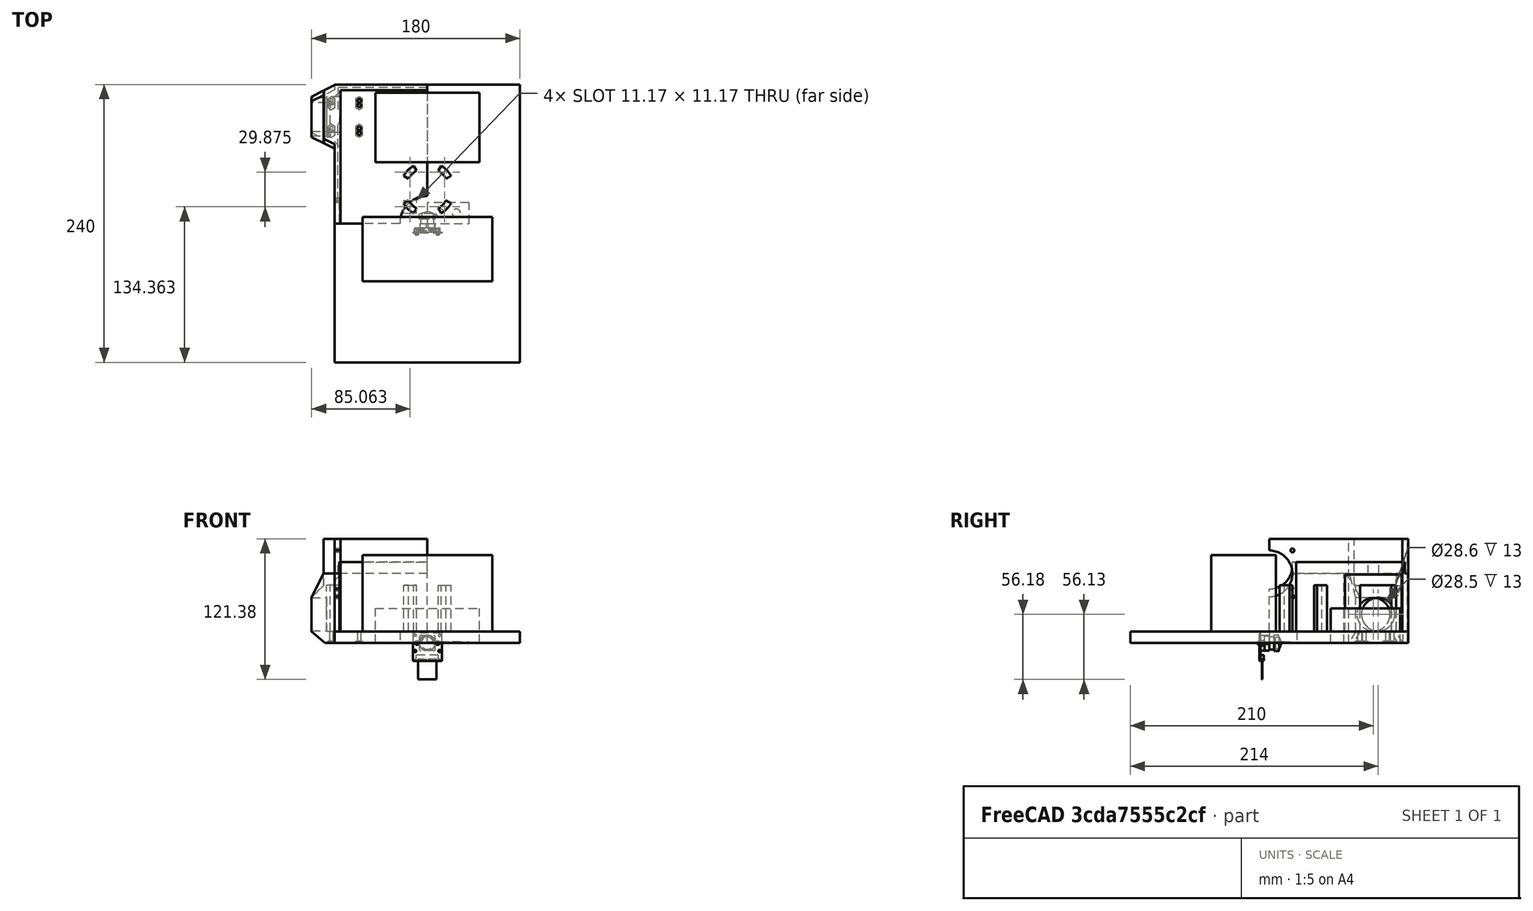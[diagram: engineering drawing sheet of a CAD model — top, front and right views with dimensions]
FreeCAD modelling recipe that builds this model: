
FCSTD DOCUMENT  (FreeCAD 0.18R16146 (Git))
Label: goat-ver3
License: All rights reserved
LicenseURL: http://en.wikipedia.org/wiki/All_rights_reserved
objects: Sketcher::SketchObject×31, PartDesign::Pocket×19, PartDesign::Pad×11, PartDesign::Body×8, Part::Feature×8, Spreadsheet::Sheet×3, PartDesign::Mirrored×3, Mesh::Feature×2, PartDesign::Chamfer×1, PartDesign::PolarPattern×1, App::Part×1, PartDesign::Plane×1, PartDesign::MultiTransform×1
note: 114 computed .brp shape members not serialized (recipe doc carries the construction recipe); baked Part::Feature solids carry a one-line shape summary decoded from their .brp

FEATURE [Spreadsheet::Sheet] Spreadsheet  label="config"
  cells = A1=NAME; B1=VALUE; A2=car_length; B2(car_length)==240mm; A3=car_width; B3==160mm; A4=lower_car_height; B4(lower_car_height)==90mm; A5=upper_car_height; B5(upper_car_height)==50mm; A6=car_floor_thickness; B6(car_floor_thickness)==10mm; A7=car_wall_thickness; B7(car_wall_thickness)==5mm; A8=car_connect_space; B8(car_connect_space)==0.5mm; A9=car_connect_magnet_radius; B9(car_connect_magnet_radius)==7.05mm; A10=car_connect_height; B10==10mm; A11=ENGINES; B11(ENGINES)=; A12=engine_radius; B12(engine_radius)==14.3mm; A13=engine_placement_from_base; B13(engine_placement_from_base)==config.car_length / 2 - 26mm; A14=engine_lift_from_base; B14(engine_lift_from_base)==0.5mm; A15=engine_house_height; B15(engine_house_height)==40mm; A16=engine_house_width; B16(engine_house_width)==30.9mm; A17=engine_house_length; B17(engine_house_length)==35mm; A18=engine_front_length; B18(engine_front_length)==20mm; A19=engine_screw_sepdist; B19(engine_screw_sepdist)==24mm; A20=engine_screw_hole_radius; B20(engine_screw_hole_radius)==1.65mm; A21=engine_screw_nut_radius; B21(engine_screw_nut_radius)==3.55mm; A22=engine_screw_nut_depth; B22(engine_screw_nut_depth)==1.8mm; A23=engine_pocket_house; B23(engine_pocket_house)==12mm; A24=FAN; A25=fan_length; B25(fan_length)==50mm; A26=fan_insert_slit_length; B26(fan_insert_slit_length)==46mm; A27=fan_screw_sepdist; B27(fan_screw_sepdist)==40mm; A28=fan_insert_depth; B28(fan_insert_depth)==1mm; A29=fan_screw_hole_radius; B29(fan_screw_hole_radius)==1.65mm; A30=fan_screw_nut_radius; B30(fan_screw_nut_radius)==3.55mm; A31=GRASSCUTTER; A32=grasscutter_motor_radius; B32(grasscutter_motor_radius)==18.7mm; A33=grasscutter_inner_radius; B33(grasscutter_inner_radius)==7.5mm; A34=grasscutter_inner_depth; B34(grasscutter_inner_depth)==4.55mm; A35=grasscutter_wall_height; B35(grasscutter_wall_height)==50mm; A36=grasscutter_screw_radius; B36(grasscutter_screw_radius)==13.5mm; A37=grasscutter_screw_circledist; B37(grasscutter_screw_circledist)==2 * 3.14 * B36 / 6; A38=grasscutter_screw_hole_radius; B38(grasscutter_screw_hole_radius)==1.52mm; A39=grasscutter_screw_nut_radius; B39(grasscutter_screw_nut_radius)==2.5mm; A40=grasscutter_screw_nut_depth; B40(grasscutter_screw_nut_depth)==1mm; A41=grasscutter_placement_yaxis; B41(grasscutter_placement_yaxis)==config.rpi_placement_yaxis - config.grasscutter_motor_radius - 5mm; A44=BATTERY; A45=battery_length; B45(battery_length)==112mm; A46=battery_width; B46(battery_width)==55.7mm; A47=battery_height; B47(battery_height)==66mm; A48=battery_placement_yaxis; B48(battery_placement_yaxis)==-config.battery_width + config.grasscutter_placement_yaxis - config.grasscutter_motor_radius - 5mm; A50=RASPBERRY; A51=rpi_height; B51(rpi_height)==30mm; A52=rpi_width; B52(rpi_width)==60mm; A53=rpi_length; B53(rpi_length)==90mm; A54=rpi_placement_yaxis; B54(rpi_placement_yaxis)==config.car_length / 2 - config.rpi_width - config.car_wall_thickness - 2mm; A57=CAMERA; B57(CAMERA)=; C57=https://www.raspberrypi-spy.co.uk/2013/05/pi-camera-module-mechanical-dimensions/; A59=camera_placement_yaxis; B59(camera_placement_yaxis)==120mm; A60=camera_placement_zaxis; B60==60mm; A61=camera_support_start_zaxis; B61(camera_support_start_zaxis)==50mm; A62=camera_tilt_angle; B62(camera_tilt_angle)=15; A63=camera_width; B63(camera_width)==24mm; A64=camera_height; B64(camera_height)==25mm; A65=camera_lens_length; B65(camera_lens_length)==13mm; A66=camera_lens_radius; B66(camera_lens_radius)==7.5mm; A67=camera_screw1_height; B67(camera_screw1_height)==9.5mm; A68=camera_screw2_height; B68(camera_screw2_height)==9.5mm + 12.5mm; A69=camera_screw_dist_apart; B69(camera_screw_dist_apart)==21mm; A70=camera_screw_radius; B70(camera_screw_radius)==1.1mm; A71=camera_screw_depth; B71==3mm; C71=length of taps to hold the camera; A72=camera_lens_placement_height; B72==24mm - 9.5mm
FEATURE [Sketcher::SketchObject] Sketch
  MapMode = 5
  Support = -> [XY_Plane]
  expr: Constraints[10] = config.car_width / 2
  expr: Constraints[9] = config.car_length / 2
  sketch-geometry (4):
    g0: LineSegment StartX=0 StartY=0 StartZ=0 EndX=-80 EndY=0 EndZ=0
    g1: LineSegment StartX=-80 StartY=0 StartZ=0 EndX=-80 EndY=120 EndZ=0
    g2: LineSegment StartX=-80 StartY=120 StartZ=0 EndX=0 EndY=120 EndZ=0
    g3: LineSegment StartX=0 StartY=120 StartZ=0 EndX=0 EndY=0 EndZ=0
  constraints (11):
    c: Coincident(g0,g1)
    c: Coincident(g1,g2)
    c: Coincident(g2,g3)
    c: Coincident(g3,g0)
    c: Horizontal(g0)
    c: Horizontal(g2)
    c: Vertical(g1)
    c: Vertical(g3)
    c: Coincident(g0,g-1)
    c: Distance(g3) = 120
    c: Distance(g2) = 80
FEATURE [PartDesign::Pad] Pad  label="pad-floor"
  Length = 10
  Length2 = 100
  Profile = -> Sketch
  Type = 0
  expr: Length = config.car_floor_thickness
FEATURE [Sketcher::SketchObject] Sketch002
  MapMode = 5
  Support = -> [XY_Plane]
  expr: Constraints[34] = config.engine_placement_from_base
  expr: Constraints[28] = config.car_width / 2
  expr: Constraints[26] = config.car_wall_thickness
  expr: Constraints[27] = config.car_wall_thickness
  expr: Constraints[25] = config.engine_front_length
  expr: Constraints[24] = config.engine_front_length / 2
  expr: Constraints[23] = config.engine_house_width
  expr: Constraints[21] = config.car_length / 2
  expr: Constraints[20] = config.car_width / 2
  sketch-geometry (12):
    g0: LineSegment StartX=0 StartY=115 StartZ=0 EndX=0 EndY=120 EndZ=0
    g1: LineSegment StartX=0 StartY=120 StartZ=0 EndX=-80 EndY=120 EndZ=0
    g2: LineSegment StartX=-80 StartY=120 StartZ=0 EndX=-80 EndY=119.45 EndZ=0
    g3: LineSegment StartX=-80 StartY=119.45 StartZ=0 EndX=-100 EndY=109.45 EndZ=0
    g4: LineSegment StartX=-100 StartY=109.45 StartZ=0 EndX=-100 EndY=78.55 EndZ=0
    g5: LineSegment StartX=-100 StartY=78.55 StartZ=0 EndX=-80 EndY=68.55 EndZ=0
    g6: LineSegment StartX=-80 StartY=68.55 StartZ=0 EndX=-80 EndY=0 EndZ=0
    g7: LineSegment StartX=-80 StartY=0 StartZ=0 EndX=-75 EndY=0 EndZ=0
    g8: LineSegment StartX=-75 StartY=0 StartZ=0 EndX=-75 EndY=115 EndZ=0
    g9: LineSegment StartX=-75 StartY=115 StartZ=0 EndX=0 EndY=115 EndZ=0
    g10: LineSegment [constr] StartX=-100 StartY=78.55 StartZ=0 EndX=-100 EndY=94 EndZ=0
    g11: LineSegment [constr] StartX=-100 StartY=94 StartZ=0 EndX=-100 EndY=109.45 EndZ=0
  constraints (35):
    c: PointOnObject(g0,g-2)
    c: Vertical(g0)
    c: Coincident(g0,g1)
    c: Horizontal(g1)
    c: Coincident(g1,g2)
    c: Vertical(g2)
    c: Coincident(g2,g3)
    c: Coincident(g3,g4)
    c: Vertical(g4)
    c: Coincident(g4,g5)
    c: Coincident(g5,g6)
    c: PointOnObject(g6,g-1)
    c: Vertical(g6)
    c: Coincident(g6,g7)
    c: PointOnObject(g7,g-1)
    c: Coincident(g7,g8)
    c: Vertical(g8)
    c: Coincident(g8,g9)
    c: Coincident(g9,g0)
    c: Horizontal(g9)
    c: Distance(g1) = 80
    c: Distance(g-1,g0) = 120
    c: Equal(g3,g5)
    c: Distance(g4) = 30.9
    c: DistanceY(g3,g2) = 10
    c: DistanceX(g3,g2) = 20
    c: Distance(g0,g0) = 5
    c: Distance(g6,g7) = 5
    c: Distance(g-1,g6) = 80
    c: Coincident(g4,g10)
    c: PointOnObject(g10,g4)
    c: Coincident(g10,g11)
    c: Coincident(g11,g3)
    c: Equal(g10,g11)
    c: DistanceY(g-1,g10) = 94
FEATURE [PartDesign::Pad] Pad001  label="pad-walls"
  BaseFeature = -> Pad
  Length = 90
  Length2 = 100
  Profile = -> Sketch002
  Type = 0
  expr: Length = config.lower_car_height
FEATURE [Sketcher::SketchObject] Sketch003
  AttachmentOffset = pos=(0,0,-75) rot=(0,0,1;0rad)
  MapMode = 5
  Placement = pos=(-75,1.67e-14,-1.67e-14) rot=(0.57735,0.57735,0.57735;2.0944rad)
  Support = -> [YZ_Plane]
  expr: AttachmentOffset.Base.y = 0
  expr: Constraints[16] = config.engine_placement_from_base
  expr: Constraints[10] = config.car_floor_thickness
  expr: Constraints[9] = config.engine_house_height
  expr: Constraints[8] = config.engine_house_width
  sketch-geometry (6):
    g0: LineSegment StartX=78.55 StartY=50 StartZ=0 EndX=109.45 EndY=50 EndZ=0
    g1: LineSegment StartX=109.45 StartY=50 StartZ=0 EndX=109.45 EndY=10 EndZ=0
    g2: LineSegment StartX=109.45 StartY=10 StartZ=0 EndX=78.55 EndY=10 EndZ=0
    g3: LineSegment StartX=78.55 StartY=10 StartZ=0 EndX=78.55 EndY=50 EndZ=0
    g4: LineSegment [constr] StartX=78.55 StartY=10 StartZ=0 EndX=94 EndY=10 EndZ=0
    g5: LineSegment [constr] StartX=94 StartY=10 StartZ=0 EndX=109.45 EndY=10 EndZ=0
  constraints (17):
    c: Coincident(g0,g1)
    c: Coincident(g1,g2)
    c: Coincident(g2,g3)
    c: Coincident(g3,g0)
    c: Horizontal(g0)
    c: Horizontal(g2)
    c: Vertical(g1)
    c: Vertical(g3)
    c: Distance(g0) = 30.9
    c: Distance(g3) = 40
    c: DistanceY(g-1,g2) = 10
    c: Coincident(g2,g4)
    c: Horizontal(g4)
    c: Coincident(g4,g5)
    c: Coincident(g5,g1)
    c: Equal(g4,g5)
    c: DistanceX(g-1,g4) = 94
FEATURE [PartDesign::Pocket] Pocket  label="pocket-engine-house"
  BaseFeature = -> Pad001
  Length = 12
  Length2 = 100
  Profile = -> Sketch003
  Type = 0
  expr: Length = config.engine_pocket_house
FEATURE [PartDesign::Pocket] Pocket001  label="pocket-engine-radius"
  BaseFeature = -> Pocket
  Length = 5
  Length2 = 100
  Type = 1
FEATURE [Sketcher::SketchObject] Sketch005
  MapMode = 5
  Support = -> [XY_Plane]
  expr: Constraints[24] = config.car_width / 2 - config.car_wall_thickness + config.engine_pocket_house
  expr: Constraints[20] = config.engine_screw_hole_radius
  expr: Constraints[15] = config.engine_placement_from_base
  expr: Constraints[14] = config.engine_screw_sepdist
  expr: Constraints[10] = config.engine_screw_hole_radius * 2.5
  sketch-geometry (10):
    g0: LineSegment [constr] StartX=-82.875 StartY=106 StartZ=0 EndX=-58.875 EndY=106 EndZ=0
    g1: LineSegment [constr] StartX=-58.875 StartY=106 StartZ=0 EndX=-58.875 EndY=82 EndZ=0
    g2: LineSegment [constr] StartX=-58.875 StartY=82 StartZ=0 EndX=-82.875 EndY=82 EndZ=0
    g3: LineSegment [constr] StartX=-82.875 StartY=82 StartZ=0 EndX=-82.875 EndY=106 EndZ=0
    g4: LineSegment [constr] StartX=-82.875 StartY=106 StartZ=0 EndX=-87 EndY=94 EndZ=0
    g5: LineSegment [constr] StartX=-87 StartY=94 StartZ=0 EndX=-82.875 EndY=82 EndZ=0
    g6: Circle CenterX=-82.875 CenterY=106 CenterZ=0 NormalX=0 NormalY=0 NormalZ=1 AngleXU=0 Radius=1.65
    g7: Circle CenterX=-58.875 CenterY=106 CenterZ=0 NormalX=0 NormalY=0 NormalZ=1 AngleXU=0 Radius=1.65
    g8: Circle CenterX=-58.875 CenterY=82 CenterZ=0 NormalX=0 NormalY=0 NormalZ=1 AngleXU=0 Radius=1.65
    g9: Circle CenterX=-82.875 CenterY=82 CenterZ=0 NormalX=0 NormalY=0 NormalZ=1 AngleXU=0 Radius=1.65
  constraints (25):
    c: Coincident(g0,g1)
    c: Coincident(g1,g2)
    c: Coincident(g2,g3)
    c: Coincident(g3,g0)
    c: Horizontal(g0)
    c: Vertical(g1)
    c: Coincident(g0,g4)
    c: Coincident(g4,g5)
    c: Coincident(g5,g2)
    c: Equal(g5,g4)
    c: DistanceX(g4,g0) = 4.125
    c: Equal(g0,g3)
    c: Equal(g3,g2)
    c: Equal(g2,g1)
    c: Distance(g1) = 24
    c: DistanceY(g-1,g4) = 94
    c: Coincident(g6,g0)
    c: Coincident(g7,g0)
    c: Coincident(g8,g1)
    c: Coincident(g9,g2)
    c: Radius(g6) = 1.65
    c: Equal(g6,g7)
    c: Equal(g6,g8)
    c: Equal(g6,g9)
    c: DistanceX(g4,g-1) = 87
FEATURE [PartDesign::Pocket] Pocket002  label="pocket-engine-screw"
  BaseFeature = -> Pocket001
  Length = 10
  Length2 = 100
  Profile = -> Sketch005
  Reversed = true
  Type = 0
  expr: Length = config.car_floor_thickness
FEATURE [Sketcher::SketchObject] Sketch006
  MapMode = 5
  Support = -> [XY_Plane]
  expr: Constraints[74] = config.engine_screw_nut_radius
  expr: Constraints[14] = config.engine_screw_sepdist
  expr: Constraints[16] = config.car_width / 2 - config.car_wall_thickness + config.engine_pocket_house
  expr: Constraints[10] = config.engine_screw_hole_radius * 2.5
  expr: Constraints[15] = config.engine_placement_from_base
  sketch-geometry (34):
    g0: LineSegment [constr] StartX=-82.875 StartY=106 StartZ=0 EndX=-58.875 EndY=106 EndZ=0
    g1: LineSegment [constr] StartX=-58.875 StartY=106 StartZ=0 EndX=-58.875 EndY=82 EndZ=0
    g2: LineSegment [constr] StartX=-58.875 StartY=82 StartZ=0 EndX=-82.875 EndY=82 EndZ=0
    g3: LineSegment [constr] StartX=-82.875 StartY=82 StartZ=0 EndX=-82.875 EndY=106 EndZ=0
    g4: LineSegment [constr] StartX=-82.875 StartY=106 StartZ=0 EndX=-87 EndY=94 EndZ=0
    g5: LineSegment [constr] StartX=-87 StartY=94 StartZ=0 EndX=-82.875 EndY=82 EndZ=0
    g6: LineSegment StartX=-79.8006 StartY=107.775 StartZ=0 EndX=-82.875 EndY=109.55 EndZ=0
    g7: LineSegment StartX=-82.875 StartY=109.55 StartZ=0 EndX=-85.9494 EndY=107.775 EndZ=0
    g8: LineSegment StartX=-85.9494 StartY=107.775 StartZ=0 EndX=-85.9494 EndY=104.225 EndZ=0
    g9: LineSegment StartX=-85.9494 StartY=104.225 StartZ=0 EndX=-82.875 EndY=102.45 EndZ=0
    g10: LineSegment StartX=-82.875 StartY=102.45 StartZ=0 EndX=-79.8006 EndY=104.225 EndZ=0
    g11: LineSegment StartX=-79.8006 StartY=104.225 StartZ=0 EndX=-79.8006 EndY=107.775 EndZ=0
    g12: Circle [constr] CenterX=-82.875 CenterY=106 CenterZ=0 NormalX=0 NormalY=0 NormalZ=1 AngleXU=0 Radius=3.55
    g13: LineSegment StartX=-55.8006 StartY=107.775 StartZ=0 EndX=-58.875 EndY=109.55 EndZ=0
    g14: LineSegment StartX=-58.875 StartY=109.55 StartZ=0 EndX=-61.9494 EndY=107.775 EndZ=0
    g15: LineSegment StartX=-61.9494 StartY=107.775 StartZ=0 EndX=-61.9494 EndY=104.225 EndZ=0
    g16: LineSegment StartX=-61.9494 StartY=104.225 StartZ=0 EndX=-58.875 EndY=102.45 EndZ=0
    g17: LineSegment StartX=-58.875 StartY=102.45 StartZ=0 EndX=-55.8006 EndY=104.225 EndZ=0
    g18: LineSegment StartX=-55.8006 StartY=104.225 StartZ=0 EndX=-55.8006 EndY=107.775 EndZ=0
    g19: Circle [constr] CenterX=-58.875 CenterY=106 CenterZ=0 NormalX=0 NormalY=0 NormalZ=1 AngleXU=0 Radius=3.55
    g20: LineSegment StartX=-58.875 StartY=85.55 StartZ=0 EndX=-61.9494 EndY=83.775 EndZ=0
    g21: LineSegment StartX=-61.9494 StartY=83.775 StartZ=0 EndX=-61.9494 EndY=80.225 EndZ=0
    g22: LineSegment StartX=-61.9494 StartY=80.225 StartZ=0 EndX=-58.875 EndY=78.45 EndZ=0
    g23: LineSegment StartX=-58.875 StartY=78.45 StartZ=0 EndX=-55.8006 EndY=80.225 EndZ=0
    g24: LineSegment StartX=-55.8006 StartY=80.225 StartZ=0 EndX=-55.8006 EndY=83.775 EndZ=0
    g25: LineSegment StartX=-55.8006 StartY=83.775 StartZ=0 EndX=-58.875 EndY=85.55 EndZ=0
    g26: Circle [constr] CenterX=-58.875 CenterY=82 CenterZ=0 NormalX=0 NormalY=0 NormalZ=1 AngleXU=0 Radius=3.55
    g27: LineSegment StartX=-79.8006 StartY=83.775 StartZ=0 EndX=-82.875 EndY=85.55 EndZ=0
    g28: LineSegment StartX=-82.875 StartY=85.55 StartZ=0 EndX=-85.9494 EndY=83.775 EndZ=0
    g29: LineSegment StartX=-85.9494 StartY=83.775 StartZ=0 EndX=-85.9494 EndY=80.225 EndZ=0
    g30: LineSegment StartX=-85.9494 StartY=80.225 StartZ=0 EndX=-82.875 EndY=78.45 EndZ=0
    g31: LineSegment StartX=-82.875 StartY=78.45 StartZ=0 EndX=-79.8006 EndY=80.225 EndZ=0
    g32: LineSegment StartX=-79.8006 StartY=80.225 StartZ=0 EndX=-79.8006 EndY=83.775 EndZ=0
    g33: Circle [constr] CenterX=-82.875 CenterY=82 CenterZ=0 NormalX=0 NormalY=0 NormalZ=1 AngleXU=0 Radius=3.55
  constraints (81):
    c: Coincident(g0,g1)
    c: Coincident(g1,g2)
    c: Coincident(g2,g3)
    c: Coincident(g3,g0)
    c: Horizontal(g0)
    c: Vertical(g1)
    c: Coincident(g0,g4)
    c: Coincident(g4,g5)
    c: Coincident(g5,g2)
    c: Equal(g5,g4)
    c: DistanceX(g4,g0) = 4.125
    c: Equal(g0,g3)
    c: Equal(g3,g2)
    c: Equal(g2,g1)
    c: Distance(g1) = 24
    c: DistanceY(g-1,g4) = 94
    c: DistanceX(g4,g-1) = 87
    c: Coincident(g6,g7)
    c: Coincident(g7,g8)
    c: Coincident(g8,g9)
    c: Coincident(g9,g10)
    c: Coincident(g10,g11)
    c: Coincident(g11,g6)
    c: Equal(g6, g7-g11) x5
    c: PointOnObject(g6,g12)
    c: PointOnObject(g7,g12)
    c: PointOnObject(g8,g12)
    c: PointOnObject(g9,g12)
    c: PointOnObject(g10,g12)
    c: PointOnObject(g11,g12)
    c: Coincident(g12,g0)
    c: Coincident(g13,g14)
    c: Coincident(g14,g15)
    c: Coincident(g15,g16)
    c: Coincident(g16,g17)
    c: Coincident(g17,g18)
    c: Coincident(g18,g13)
    c: Equal(g13, g14-g18) x5
    c: PointOnObject(g13,g19)
    c: PointOnObject(g14,g19)
    c: PointOnObject(g15,g19)
    c: PointOnObject(g16,g19)
    c: PointOnObject(g17,g19)
    c: PointOnObject(g18,g19)
    c: Coincident(g19,g0)
    c: Coincident(g20,g21)
    c: Coincident(g21,g22)
    c: Coincident(g22,g23)
    c: Coincident(g23,g24)
    c: Coincident(g24,g25)
    c: Coincident(g25,g20)
    c: Equal(g20, g21-g25) x5
    c: PointOnObject(g20,g26)
    c: PointOnObject(g21,g26)
    c: PointOnObject(g22,g26)
    c: PointOnObject(g23,g26)
    c: PointOnObject(g24,g26)
    c: PointOnObject(g25,g26)
    c: Coincident(g26,g1)
    c: Vertical(g8)
    c: Vertical(g21)
    c: Vertical(g15)
    c: Radius(g26) = 3.55
    c: Equal(g26,g19)
    c: Equal(g26,g12)
    c: Coincident(g27,g28)
    c: Coincident(g28,g29)
    c: Coincident(g29,g30)
    c: Coincident(g30,g31)
    c: Coincident(g31,g32)
    c: Coincident(g32,g27)
    c: Equal(g27, g28-g32) x5
    c: PointOnObject(g27,g33)
    c: PointOnObject(g28,g33)
    c: PointOnObject(g29,g33)
    c: PointOnObject(g30,g33)
    c: PointOnObject(g31,g33)
    c: PointOnObject(g32,g33)
    c: Coincident(g33,g2)
    c: Vertical(g29)
    c: Equal(g33,g12)
FEATURE [PartDesign::Pocket] Pocket003  label="pocket-engine-nut"
  BaseFeature = -> Pocket002
  Length = 1.8
  Length2 = 100
  Profile = -> Sketch006
  Reversed = true
  Type = 0
FEATURE [Sketcher::SketchObject] Sketch007
  MapMode = 5
  Placement = pos=(0,0,0) rot=(1,0,0;1.5708rad)
  Support = -> [XZ_Plane]
  expr: Constraints[17] = config.car_floor_thickness + 2 * config.engine_radius + config.engine_lift_from_base * 2
  expr: Constraints[16] = config.car_width / 2 + config.engine_pocket_house * 0.8
  expr: Constraints[10] = config.car_floor_thickness
  expr: Constraints[13] = config.lower_car_height
  expr: Constraints[12] = config.car_width / 2 + config.engine_front_length
  sketch-geometry (6):
    g0: LineSegment StartX=-89.6 StartY=90 StartZ=0 EndX=-100 EndY=39.6 EndZ=0
    g1: LineSegment StartX=-100 StartY=39.6 StartZ=0 EndX=-100 EndY=90 EndZ=0
    g2: LineSegment StartX=-100 StartY=90 StartZ=0 EndX=-89.6 EndY=90 EndZ=0
    g3: LineSegment StartX=-88.4 StartY=0 StartZ=0 EndX=-100 EndY=10 EndZ=0
    g4: LineSegment StartX=-100 StartY=10 StartZ=0 EndX=-100 EndY=0 EndZ=0
    g5: LineSegment StartX=-100 StartY=0 StartZ=0 EndX=-88.4 EndY=0 EndZ=0
  constraints (18):
    c: Coincident(g0,g1)
    c: Vertical(g1)
    c: Coincident(g1,g2)
    c: Coincident(g2,g0)
    c: Horizontal(g2)
    c: PointOnObject(g3,g-1)
    c: Coincident(g3,g4)
    c: PointOnObject(g4,g-1)
    c: Coincident(g4,g5)
    c: Coincident(g5,g3)
    c: Distance(g4) = 10
    c: DistanceX(g4,g-1) = 100
    c: DistanceX(g1,g-1) = 100
    c: DistanceY(g-1,g1) = 90
    c: DistanceX(g3,g-1) = 88.4
    c: Vertical(g4)
    c: DistanceX(g0,g-1) = 89.6
    c: DistanceY(g4,g0) = 39.6
FEATURE [PartDesign::Pocket] Pocket004  label="pocket-trim-engine-house"
  BaseFeature = -> Pocket003
  Length = 5
  Length2 = 100
  Profile = -> Sketch007
  Type = 1
FEATURE [Sketcher::SketchObject] Sketch009
  MapMode = 5
  Support = -> [XY_Plane]
  expr: Constraints[0] = config.grasscutter_motor_radius + config.car_wall_thickness
  sketch-geometry (1):
    g0: Circle CenterX=0 CenterY=0 CenterZ=0 NormalX=0 NormalY=0 NormalZ=1 AngleXU=0 Radius=23.7
  constraints (1):
    c: Radius(g0) = 23.7
FEATURE [PartDesign::Pocket] Pocket005  label="pocket-for-grasscutter"
  BaseFeature = -> Pocket004
  Length = 5
  Length2 = 100
  Profile = -> Sketch009
  Reversed = true
  Type = 1
FEATURE [Sketcher::SketchObject] Sketch014
  AttachmentOffset = pos=(0,0,90) rot=(0,0,1;0rad)
  MapMode = 5
  Placement = pos=(0,0,90) rot=(0,0,1;0rad)
  Support = -> [XY_Plane]
  expr: Constraints[26] = config.car_connect_magnet_radius + 0.5mm
  expr: Constraints[25] = config.engine_placement_from_base
  expr: Constraints[23] = config.car_connect_magnet_radius
  expr: Constraints[17] = (config.car_wall_thickness - config.car_connect_space) / 2
  expr: AttachmentOffset.Base.z = config.lower_car_height
  expr: Constraints[16] = config.car_length / 2 - config.car_wall_thickness
  expr: Constraints[15] = config.car_width / 2 - config.car_wall_thickness
  expr: Constraints[13] = (config.car_wall_thickness - config.car_connect_space) / 2
  sketch-geometry (9):
    g0: LineSegment StartX=0 StartY=115 StartZ=0 EndX=0 EndY=117.25 EndZ=0
    g1: LineSegment StartX=0 StartY=117.25 StartZ=0 EndX=-77.25 EndY=117.25 EndZ=0
    g2: LineSegment StartX=-77.25 StartY=117.25 StartZ=0 EndX=-77.25 EndY=98.6489 EndZ=0
    g3: LineSegment StartX=-77.25 StartY=0 StartZ=0 EndX=-75 EndY=0 EndZ=0
    g4: LineSegment StartX=-75 StartY=0 StartZ=0 EndX=-75 EndY=115 EndZ=0
    g5: LineSegment StartX=-75 StartY=115 StartZ=0 EndX=0 EndY=115 EndZ=0
    g6: LineSegment StartX=-77.25 StartY=0 StartZ=0 EndX=-77.25 EndY=89.3511 EndZ=0
    g7: LineSegment [constr] StartX=-77.25 StartY=98.6489 StartZ=0 EndX=-77.25 EndY=89.3511 EndZ=0
    g8: ArcOfCircle CenterX=-82.55 CenterY=94 CenterZ=0 NormalX=0 NormalY=0 NormalZ=1 AngleXU=0 Radius=7.05 StartAngle=5.56314 EndAngle=7.00323
  constraints (27):
    c: PointOnObject(g0,g-2)
    c: PointOnObject(g0,g-2)
    c: Coincident(g0,g1)
    c: Horizontal(g1)
    c: Coincident(g1,g2)
    c: Vertical(g2)
    c: Coincident(g3,g4)
    c: Vertical(g4)
    c: Coincident(g4,g5)
    c: Coincident(g5,g0)
    c: Horizontal(g5)
    c: PointOnObject(g3,g-1)
    c: PointOnObject(g3,g-1)
    c: DistanceX(g3,g3) = 2.25
    c: DistanceY(g0,g0) = 2.25
    c: DistanceX(g3,g-1) = 75
    c: DistanceY(g-1,g0) = 115
    c: DistanceX(g1,g4) = 2.25
    c: Coincident(g3,g6)
    c: Vertical(g6)
    c: Coincident(g7,g2)
    c: Coincident(g7,g6)
    c: Coincident(g8,g2)
    c: Radius(g8) = 7.05
    c: Coincident(g8,g6)
    c: DistanceY(g-1,g8) = 94
    c: Distance(g8,g4) = 7.55
FEATURE [PartDesign::Pad] Pad004  label="Pad-connector"
  BaseFeature = -> Pocket005
  Length = 10
  Length2 = 100
  Profile = -> Sketch014
  Type = 0
FEATURE [Sketcher::SketchObject] Sketch016
  MapMode = 5
  Placement = pos=(0,0,0) rot=(0.57735,0.57735,0.57735;2.0944rad)
  Support = -> [YZ_Plane]
  expr: Constraints[10] = config.fan_screw_sepdist / 2
  expr: Constraints[18] = config.fan_screw_hole_radius
  expr: Constraints[9] = config.fan_screw_sepdist
  expr: Constraints[8] = config.lower_car_height - config.fan_screw_hole_radius * 2
  sketch-geometry (8):
    g0: LineSegment [constr] StartX=-3.7e-15 StartY=86.7 StartZ=0 EndX=20 EndY=86.7 EndZ=0
    g1: LineSegment [constr] StartX=20 StartY=86.7 StartZ=0 EndX=20 EndY=46.7 EndZ=0
    g2: LineSegment [constr] StartX=20 StartY=46.7 StartZ=0 EndX=-3.6e-15 EndY=46.7 EndZ=0
    g3: LineSegment [constr] StartX=-3.7e-15 StartY=46.7 StartZ=0 EndX=-3.7e-15 EndY=86.7 EndZ=0
    g4: ArcOfCircle CenterX=0 CenterY=66.7 CenterZ=0 NormalX=0 NormalY=0 NormalZ=1 AngleXU=0 Radius=20 StartAngle=4.71239 EndAngle=7.85398
    g5: LineSegment StartX=-3.7e-15 StartY=86.7 StartZ=0 EndX=-3.7e-15 EndY=46.7 EndZ=0
    g6: Circle CenterX=20 CenterY=86.7 CenterZ=0 NormalX=0 NormalY=0 NormalZ=1 AngleXU=0 Radius=1.65
    g7: Circle CenterX=20 CenterY=46.7 CenterZ=0 NormalX=0 NormalY=0 NormalZ=1 AngleXU=0 Radius=1.65
  constraints (21):
    c: Coincident(g0,g1)
    c: Coincident(g1,g2)
    c: Coincident(g2,g3)
    c: Coincident(g3,g0)
    c: Horizontal(g0)
    c: Horizontal(g2)
    c: Vertical(g1)
    c: Vertical(g3)
    c: DistanceY(g-1,g0) = 86.7
    c: Distance(g1) = 40
    c: Distance(g0) = 20
    c: PointOnObject(g4,g3)
    c: Coincident(g4,g0)
    c: Coincident(g5,g4)
    c: Coincident(g6,g0)
    c: Coincident(g7,g1)
    c: Coincident(g2,g4)
    c: Coincident(g2,g5)
    c: Radius(g6) = 1.65
    c: Equal(g6,g7)
    c: PointOnObject(g4,g-2)
FEATURE [PartDesign::Pocket] Pocket009  label="Pocket-fan-opening"
  BaseFeature = -> Pad004
  Length = 5
  Length2 = 100
  Profile = -> Sketch016
  Type = 1
FEATURE [Sketcher::SketchObject] Sketch017
  AttachmentOffset = pos=(0,0,-75) rot=(0,0,1;0rad)
  MapMode = 5
  Placement = pos=(-75,1.67e-14,-1.67e-14) rot=(0.57735,0.57735,0.57735;2.0944rad)
  Support = -> [YZ_Plane]
  expr: AttachmentOffset.Base.z = -config.car_width / 2 + config.car_wall_thickness
  expr: Constraints[11] = config.fan_insert_slit_length / 2 + 0.3mm
  expr: Constraints[10] = config.car_floor_thickness
  expr: Constraints[9] = config.lower_car_height + 0.3mm
  sketch-geometry (4):
    g0: LineSegment StartX=0 StartY=90.3 StartZ=0 EndX=23.3 EndY=90.3 EndZ=0
    g1: LineSegment StartX=23.3 StartY=90.3 StartZ=0 EndX=23.3 EndY=10 EndZ=0
    g2: LineSegment StartX=23.3 StartY=10 StartZ=0 EndX=0 EndY=10 EndZ=0
    g3: LineSegment StartX=0 StartY=10 StartZ=0 EndX=0 EndY=90.3 EndZ=0
  constraints (12):
    c: Coincident(g0,g1)
    c: Coincident(g1,g2)
    c: Coincident(g2,g3)
    c: Coincident(g3,g0)
    c: Horizontal(g0)
    c: Horizontal(g2)
    c: Vertical(g1)
    c: Vertical(g3)
    c: PointOnObject(g0,g-2)
    c: DistanceY(g-1,g0) = 90.3
    c: DistanceY(g-1,g2) = 10
    c: DistanceX(g0,g0) = 23.3
FEATURE [PartDesign::Pocket] Pocket010  label="pocket-fan-slit"
  BaseFeature = -> Pocket009
  Length = 1
  Length2 = 100
  Profile = -> Sketch017
  Type = 0
  expr: Length = config.fan_insert_depth
FEATURE [Sketcher::SketchObject] Sketch018
  AttachmentOffset = pos=(0,0,10) rot=(0,0,1;0rad)
  MapMode = 5
  Placement = pos=(0,0,10) rot=(0,0,1;0rad)
  Support = -> [XY_Plane002]
  expr: Constraints[13] = config.battery_placement_yaxis
  expr: Constraints[11] = config.battery_length / 2
  expr: Constraints[9] = config.battery_width
  expr: AttachmentOffset.Base.y = 0
  expr: AttachmentOffset.Base.x = 0
  expr: AttachmentOffset.Base.z = config.car_floor_thickness
  expr: Constraints[7] = config.battery_length
  sketch-geometry (5):
    g0: LineSegment StartX=-56 StartY=5.6 StartZ=0 EndX=56 EndY=5.6 EndZ=0
    g1: LineSegment StartX=56 StartY=5.6 StartZ=0 EndX=56 EndY=-50.1 EndZ=0
    g2: LineSegment StartX=56 StartY=-50.1 StartZ=0 EndX=-56 EndY=-50.1 EndZ=0
    g3: LineSegment StartX=-56 StartY=-50.1 StartZ=0 EndX=-56 EndY=5.6 EndZ=0
    g4: GeomPoint X=0 Y=-50.1 Z=0
  constraints (14):
    c: Coincident(g0,g1)
    c: Coincident(g1,g2)
    c: Coincident(g2,g3)
    c: Coincident(g3,g0)
    c: Horizontal(g0)
    c: Horizontal(g2)
    c: Vertical(g3)
    c: Distance(g0) = 112
    c: Vertical(g1)
    c: Distance(g1) = 55.7
    c: PointOnObject(g4,g2)
    c: Distance(g4,g2) = 56
    c: PointOnObject(g4,g-2)
    c: DistanceY(g-1,g4) = -50.1
FEATURE [PartDesign::Pad] Pad005
  Length = 66
  Length2 = 100
  Profile = -> Sketch018
  Type = 0
  expr: Length = config.battery_height
FEATURE [PartDesign::Body] Body002  label="body-battery"
  Group = -> [Sketch018,Pad005]
  Origin = -> Origin002
  Tip = -> Pad005
FEATURE [PartDesign::Chamfer] Chamfer
  Base = -> Pocket010 [Edge83,Edge84,Edge85]
  BaseFeature = -> Pocket010
  Size = 9
FEATURE [PartDesign::Body] Body  label="Body-q11-lower"
  Group = -> [Sketch,Pad,Sketch002,Pad001,Sketch003,Pocket,Pocket001,Sketch005,Pocket002,Sketch006,Pocket003,Sketch007,Pocket004,Sketch009,Pocket005,Sketch014,Pad004,Sketch016,Pocket009,Sketch017,Pocket010,Chamfer]
  Origin = -> Origin
  Tip = -> Chamfer
FEATURE [Sketcher::SketchObject] Sketch021
  MapMode = 5
  Support = -> [XY_Plane004]
  expr: Constraints[8] = config.car_width
  expr: Constraints[7] = config.car_length
  sketch-geometry (7):
    g0: LineSegment StartX=-80 StartY=120 StartZ=0 EndX=80 EndY=120 EndZ=0
    g1: LineSegment StartX=80 StartY=120 StartZ=0 EndX=80 EndY=-120 EndZ=0
    g2: LineSegment StartX=80 StartY=-120 StartZ=0 EndX=-80 EndY=-120 EndZ=0
    g3: LineSegment StartX=-80 StartY=-120 StartZ=0 EndX=-80 EndY=120 EndZ=0
    g4: LineSegment [constr] StartX=-80 StartY=-120 StartZ=0 EndX=80 EndY=120 EndZ=0
    g5: LineSegment [constr] StartX=-80 StartY=120 StartZ=0 EndX=80 EndY=-120 EndZ=0
    g6: GeomPoint X=0 Y=0 Z=0
  constraints (17):
    c: Coincident(g0,g1)
    c: Coincident(g1,g2)
    c: Coincident(g2,g3)
    c: Horizontal(g0)
    c: Horizontal(g2)
    c: Vertical(g1)
    c: Vertical(g3)
    c: Distance(g3) = 240
    c: Distance(g0) = 160
    c: Coincident(g3,g0)
    c: Coincident(g4,g2)
    c: Coincident(g4,g0)
    c: Coincident(g5,g0)
    c: Coincident(g5,g1)
    c: PointOnObject(g6,g4)
    c: PointOnObject(g6,g5)
    c: Coincident(g6,g-1)
FEATURE [PartDesign::Pad] Pad006  label="pad-floor002"
  Length = 10
  Length2 = 100
  Profile = -> Sketch021
  Type = 0
  expr: Length = config.car_floor_thickness
FEATURE [Sketcher::SketchObject] Sketch022
  MapMode = 5
  Support = -> [XY_Plane004]
  expr: Constraints[34] = config.engine_placement_from_base
  expr: Constraints[28] = config.car_width / 2
  expr: Constraints[26] = config.car_wall_thickness
  expr: Constraints[27] = config.car_wall_thickness
  expr: Constraints[25] = config.engine_front_length
  expr: Constraints[24] = config.engine_front_length / 2
  expr: Constraints[23] = config.engine_house_width
  expr: Constraints[21] = config.car_length / 2
  expr: Constraints[20] = config.car_width / 2
  sketch-geometry (12):
    g0: LineSegment StartX=0 StartY=115 StartZ=0 EndX=0 EndY=120 EndZ=0
    g1: LineSegment StartX=0 StartY=120 StartZ=0 EndX=-80 EndY=120 EndZ=0
    g2: LineSegment StartX=-80 StartY=120 StartZ=0 EndX=-80 EndY=119.45 EndZ=0
    g3: LineSegment StartX=-80 StartY=119.45 StartZ=0 EndX=-100 EndY=109.45 EndZ=0
    g4: LineSegment StartX=-100 StartY=109.45 StartZ=0 EndX=-100 EndY=78.55 EndZ=0
    g5: LineSegment StartX=-100 StartY=78.55 StartZ=0 EndX=-80 EndY=68.55 EndZ=0
    g6: LineSegment StartX=-80 StartY=68.55 StartZ=0 EndX=-80 EndY=0 EndZ=0
    g7: LineSegment StartX=-80 StartY=0 StartZ=0 EndX=-75 EndY=0 EndZ=0
    g8: LineSegment StartX=-75 StartY=0 StartZ=0 EndX=-75 EndY=115 EndZ=0
    g9: LineSegment StartX=-75 StartY=115 StartZ=0 EndX=0 EndY=115 EndZ=0
    g10: LineSegment [constr] StartX=-100 StartY=78.55 StartZ=0 EndX=-100 EndY=94 EndZ=0
    g11: LineSegment [constr] StartX=-100 StartY=94 StartZ=0 EndX=-100 EndY=109.45 EndZ=0
  constraints (35):
    c: PointOnObject(g0,g-2)
    c: Vertical(g0)
    c: Coincident(g0,g1)
    c: Horizontal(g1)
    c: Coincident(g1,g2)
    c: Vertical(g2)
    c: Coincident(g2,g3)
    c: Coincident(g3,g4)
    c: Vertical(g4)
    c: Coincident(g4,g5)
    c: Coincident(g5,g6)
    c: PointOnObject(g6,g-1)
    c: Vertical(g6)
    c: Coincident(g6,g7)
    c: PointOnObject(g7,g-1)
    c: Coincident(g7,g8)
    c: Vertical(g8)
    c: Coincident(g8,g9)
    c: Coincident(g9,g0)
    c: Horizontal(g9)
    c: Distance(g1) = 80
    c: Distance(g-1,g0) = 120
    c: Equal(g3,g5)
    c: Distance(g4) = 30.9
    c: DistanceY(g3,g2) = 10
    c: DistanceX(g3,g2) = 20
    c: Distance(g0,g0) = 5
    c: Distance(g6,g7) = 5
    c: Distance(g-1,g6) = 80
    c: Coincident(g4,g10)
    c: PointOnObject(g10,g4)
    c: Coincident(g10,g11)
    c: Coincident(g11,g3)
    c: Equal(g10,g11)
    c: DistanceY(g-1,g10) = 94
FEATURE [PartDesign::Pad] Pad007  label="pad-wall-q11"
  BaseFeature = -> Pad006
  Length = 90
  Length2 = 100
  Profile = -> Sketch022
  Type = 0
  expr: Length = config.lower_car_height
FEATURE [Sketcher::SketchObject] Sketch023
  AttachmentOffset = pos=(0,0,-75) rot=(0,0,1;0rad)
  MapMode = 5
  Placement = pos=(-75,1.67e-14,-1.67e-14) rot=(0.57735,0.57735,0.57735;2.0944rad)
  Support = -> [YZ_Plane004]
  expr: AttachmentOffset.Base.y = 0
  expr: Constraints[16] = config.engine_placement_from_base
  expr: Constraints[10] = config.car_floor_thickness
  expr: Constraints[9] = config.engine_house_height
  expr: Constraints[8] = config.engine_house_width
  sketch-geometry (6):
    g0: LineSegment StartX=78.55 StartY=50 StartZ=0 EndX=109.45 EndY=50 EndZ=0
    g1: LineSegment StartX=109.45 StartY=50 StartZ=0 EndX=109.45 EndY=10 EndZ=0
    g2: LineSegment StartX=109.45 StartY=10 StartZ=0 EndX=78.55 EndY=10 EndZ=0
    g3: LineSegment StartX=78.55 StartY=10 StartZ=0 EndX=78.55 EndY=50 EndZ=0
    g4: LineSegment [constr] StartX=78.55 StartY=10 StartZ=0 EndX=94 EndY=10 EndZ=0
    g5: LineSegment [constr] StartX=94 StartY=10 StartZ=0 EndX=109.45 EndY=10 EndZ=0
  constraints (17):
    c: Coincident(g0,g1)
    c: Coincident(g1,g2)
    c: Coincident(g2,g3)
    c: Coincident(g3,g0)
    c: Horizontal(g0)
    c: Horizontal(g2)
    c: Vertical(g1)
    c: Vertical(g3)
    c: Distance(g0) = 30.9
    c: Distance(g3) = 40
    c: DistanceY(g-1,g2) = 10
    c: Coincident(g2,g4)
    c: Horizontal(g4)
    c: Coincident(g4,g5)
    c: Coincident(g5,g1)
    c: Equal(g4,g5)
    c: DistanceX(g-1,g4) = 94
FEATURE [PartDesign::Pocket] Pocket011  label="pocket-engine-house001"
  BaseFeature = -> Pad007
  Length = 12
  Length2 = 100
  Profile = -> Sketch023
  Type = 0
  expr: Length = config.engine_pocket_house
FEATURE [Sketcher::SketchObject] Sketch024
  MapMode = 5
  Placement = pos=(0,0,0) rot=(0.57735,0.57735,0.57735;2.0944rad)
  Support = -> [YZ_Plane004]
  expr: Constraints[2] = config.engine_radius
  expr: Constraints[1] = config.engine_placement_from_base
  expr: Constraints[0] = config.car_floor_thickness + config.engine_lift_from_base + config.engine_radius
  sketch-geometry (1):
    g0: Circle CenterX=94 CenterY=24.8 CenterZ=0 NormalX=0 NormalY=0 NormalZ=1 AngleXU=0 Radius=14.3
  constraints (3):
    c: DistanceY(g-1,g0) = 24.8
    c: DistanceX(g-1,g0) = 94
    c: Radius(g0) = 14.3
FEATURE [PartDesign::Pocket] Pocket012  label="pocket-engine-hole"
  BaseFeature = -> Pocket011
  Length = 5
  Length2 = 100
  Profile = -> Sketch024
  Type = 1
FEATURE [Sketcher::SketchObject] Sketch025
  MapMode = 5
  Support = -> [XY_Plane004]
  expr: Constraints[24] = config.car_width / 2 - config.car_wall_thickness + config.engine_pocket_house
  expr: Constraints[20] = config.engine_screw_hole_radius
  expr: Constraints[15] = config.engine_placement_from_base
  expr: Constraints[14] = config.engine_screw_sepdist
  expr: Constraints[10] = config.engine_screw_hole_radius * 2.5
  sketch-geometry (10):
    g0: LineSegment [constr] StartX=-82.875 StartY=106 StartZ=0 EndX=-58.875 EndY=106 EndZ=0
    g1: LineSegment [constr] StartX=-58.875 StartY=106 StartZ=0 EndX=-58.875 EndY=82 EndZ=0
    g2: LineSegment [constr] StartX=-58.875 StartY=82 StartZ=0 EndX=-82.875 EndY=82 EndZ=0
    g3: LineSegment [constr] StartX=-82.875 StartY=82 StartZ=0 EndX=-82.875 EndY=106 EndZ=0
    g4: LineSegment [constr] StartX=-82.875 StartY=106 StartZ=0 EndX=-87 EndY=94 EndZ=0
    g5: LineSegment [constr] StartX=-87 StartY=94 StartZ=0 EndX=-82.875 EndY=82 EndZ=0
    g6: Circle CenterX=-82.875 CenterY=106 CenterZ=0 NormalX=0 NormalY=0 NormalZ=1 AngleXU=0 Radius=1.65
    g7: Circle CenterX=-58.875 CenterY=106 CenterZ=0 NormalX=0 NormalY=0 NormalZ=1 AngleXU=0 Radius=1.65
    g8: Circle CenterX=-58.875 CenterY=82 CenterZ=0 NormalX=0 NormalY=0 NormalZ=1 AngleXU=0 Radius=1.65
    g9: Circle CenterX=-82.875 CenterY=82 CenterZ=0 NormalX=0 NormalY=0 NormalZ=1 AngleXU=0 Radius=1.65
  constraints (25):
    c: Coincident(g0,g1)
    c: Coincident(g1,g2)
    c: Coincident(g2,g3)
    c: Coincident(g3,g0)
    c: Horizontal(g0)
    c: Vertical(g1)
    c: Coincident(g0,g4)
    c: Coincident(g4,g5)
    c: Coincident(g5,g2)
    c: Equal(g5,g4)
    c: DistanceX(g4,g0) = 4.125
    c: Equal(g0,g3)
    c: Equal(g3,g2)
    c: Equal(g2,g1)
    c: Distance(g1) = 24
    c: DistanceY(g-1,g4) = 94
    c: Coincident(g6,g0)
    c: Coincident(g7,g0)
    c: Coincident(g8,g1)
    c: Coincident(g9,g2)
    c: Radius(g6) = 1.65
    c: Equal(g6,g7)
    c: Equal(g6,g8)
    c: Equal(g6,g9)
    c: DistanceX(g4,g-1) = 87
FEATURE [PartDesign::Pocket] Pocket013  label="pocket-engine-screws"
  BaseFeature = -> Pocket012
  Length = 10
  Length2 = 100
  Profile = -> Sketch025
  Reversed = true
  Type = 0
  expr: Length = config.car_floor_thickness
FEATURE [Sketcher::SketchObject] Sketch026
  MapMode = 5
  Support = -> [XY_Plane004]
  expr: Constraints[74] = config.engine_screw_nut_radius
  expr: Constraints[14] = config.engine_screw_sepdist
  expr: Constraints[16] = config.car_width / 2 - config.car_wall_thickness + config.engine_pocket_house
  expr: Constraints[10] = config.engine_screw_hole_radius * 2.5
  expr: Constraints[15] = config.engine_placement_from_base
  sketch-geometry (34):
    g0: LineSegment [constr] StartX=-82.875 StartY=106 StartZ=0 EndX=-58.875 EndY=106 EndZ=0
    g1: LineSegment [constr] StartX=-58.875 StartY=106 StartZ=0 EndX=-58.875 EndY=82 EndZ=0
    g2: LineSegment [constr] StartX=-58.875 StartY=82 StartZ=0 EndX=-82.875 EndY=82 EndZ=0
    g3: LineSegment [constr] StartX=-82.875 StartY=82 StartZ=0 EndX=-82.875 EndY=106 EndZ=0
    g4: LineSegment [constr] StartX=-82.875 StartY=106 StartZ=0 EndX=-87 EndY=94 EndZ=0
    g5: LineSegment [constr] StartX=-87 StartY=94 StartZ=0 EndX=-82.875 EndY=82 EndZ=0
    g6: LineSegment StartX=-79.8006 StartY=107.775 StartZ=0 EndX=-82.875 EndY=109.55 EndZ=0
    g7: LineSegment StartX=-82.875 StartY=109.55 StartZ=0 EndX=-85.9494 EndY=107.775 EndZ=0
    g8: LineSegment StartX=-85.9494 StartY=107.775 StartZ=0 EndX=-85.9494 EndY=104.225 EndZ=0
    g9: LineSegment StartX=-85.9494 StartY=104.225 StartZ=0 EndX=-82.875 EndY=102.45 EndZ=0
    g10: LineSegment StartX=-82.875 StartY=102.45 StartZ=0 EndX=-79.8006 EndY=104.225 EndZ=0
    g11: LineSegment StartX=-79.8006 StartY=104.225 StartZ=0 EndX=-79.8006 EndY=107.775 EndZ=0
    g12: Circle [constr] CenterX=-82.875 CenterY=106 CenterZ=0 NormalX=0 NormalY=0 NormalZ=1 AngleXU=0 Radius=3.55
    g13: LineSegment StartX=-55.8006 StartY=107.775 StartZ=0 EndX=-58.875 EndY=109.55 EndZ=0
    g14: LineSegment StartX=-58.875 StartY=109.55 StartZ=0 EndX=-61.9494 EndY=107.775 EndZ=0
    g15: LineSegment StartX=-61.9494 StartY=107.775 StartZ=0 EndX=-61.9494 EndY=104.225 EndZ=0
    g16: LineSegment StartX=-61.9494 StartY=104.225 StartZ=0 EndX=-58.875 EndY=102.45 EndZ=0
    g17: LineSegment StartX=-58.875 StartY=102.45 StartZ=0 EndX=-55.8006 EndY=104.225 EndZ=0
    g18: LineSegment StartX=-55.8006 StartY=104.225 StartZ=0 EndX=-55.8006 EndY=107.775 EndZ=0
    g19: Circle [constr] CenterX=-58.875 CenterY=106 CenterZ=0 NormalX=0 NormalY=0 NormalZ=1 AngleXU=0 Radius=3.55
    g20: LineSegment StartX=-58.875 StartY=85.55 StartZ=0 EndX=-61.9494 EndY=83.775 EndZ=0
    g21: LineSegment StartX=-61.9494 StartY=83.775 StartZ=0 EndX=-61.9494 EndY=80.225 EndZ=0
    g22: LineSegment StartX=-61.9494 StartY=80.225 StartZ=0 EndX=-58.875 EndY=78.45 EndZ=0
    g23: LineSegment StartX=-58.875 StartY=78.45 StartZ=0 EndX=-55.8006 EndY=80.225 EndZ=0
    g24: LineSegment StartX=-55.8006 StartY=80.225 StartZ=0 EndX=-55.8006 EndY=83.775 EndZ=0
    g25: LineSegment StartX=-55.8006 StartY=83.775 StartZ=0 EndX=-58.875 EndY=85.55 EndZ=0
    g26: Circle [constr] CenterX=-58.875 CenterY=82 CenterZ=0 NormalX=0 NormalY=0 NormalZ=1 AngleXU=0 Radius=3.55
    g27: LineSegment StartX=-79.8006 StartY=83.775 StartZ=0 EndX=-82.875 EndY=85.55 EndZ=0
    g28: LineSegment StartX=-82.875 StartY=85.55 StartZ=0 EndX=-85.9494 EndY=83.775 EndZ=0
    g29: LineSegment StartX=-85.9494 StartY=83.775 StartZ=0 EndX=-85.9494 EndY=80.225 EndZ=0
    g30: LineSegment StartX=-85.9494 StartY=80.225 StartZ=0 EndX=-82.875 EndY=78.45 EndZ=0
    g31: LineSegment StartX=-82.875 StartY=78.45 StartZ=0 EndX=-79.8006 EndY=80.225 EndZ=0
    g32: LineSegment StartX=-79.8006 StartY=80.225 StartZ=0 EndX=-79.8006 EndY=83.775 EndZ=0
    g33: Circle [constr] CenterX=-82.875 CenterY=82 CenterZ=0 NormalX=0 NormalY=0 NormalZ=1 AngleXU=0 Radius=3.55
  constraints (81):
    c: Coincident(g0,g1)
    c: Coincident(g1,g2)
    c: Coincident(g2,g3)
    c: Coincident(g3,g0)
    c: Horizontal(g0)
    c: Vertical(g1)
    c: Coincident(g0,g4)
    c: Coincident(g4,g5)
    c: Coincident(g5,g2)
    c: Equal(g5,g4)
    c: DistanceX(g4,g0) = 4.125
    c: Equal(g0,g3)
    c: Equal(g3,g2)
    c: Equal(g2,g1)
    c: Distance(g1) = 24
    c: DistanceY(g-1,g4) = 94
    c: DistanceX(g4,g-1) = 87
    c: Coincident(g6,g7)
    c: Coincident(g7,g8)
    c: Coincident(g8,g9)
    c: Coincident(g9,g10)
    c: Coincident(g10,g11)
    c: Coincident(g11,g6)
    c: Equal(g6, g7-g11) x5
    c: PointOnObject(g6,g12)
    c: PointOnObject(g7,g12)
    c: PointOnObject(g8,g12)
    c: PointOnObject(g9,g12)
    c: PointOnObject(g10,g12)
    c: PointOnObject(g11,g12)
    c: Coincident(g12,g0)
    c: Coincident(g13,g14)
    c: Coincident(g14,g15)
    c: Coincident(g15,g16)
    c: Coincident(g16,g17)
    c: Coincident(g17,g18)
    c: Coincident(g18,g13)
    c: Equal(g13, g14-g18) x5
    c: PointOnObject(g13,g19)
    c: PointOnObject(g14,g19)
    c: PointOnObject(g15,g19)
    c: PointOnObject(g16,g19)
    c: PointOnObject(g17,g19)
    c: PointOnObject(g18,g19)
    c: Coincident(g19,g0)
    c: Coincident(g20,g21)
    c: Coincident(g21,g22)
    c: Coincident(g22,g23)
    c: Coincident(g23,g24)
    c: Coincident(g24,g25)
    c: Coincident(g25,g20)
    c: Equal(g20, g21-g25) x5
    c: PointOnObject(g20,g26)
    c: PointOnObject(g21,g26)
    c: PointOnObject(g22,g26)
    c: PointOnObject(g23,g26)
    c: PointOnObject(g24,g26)
    c: PointOnObject(g25,g26)
    c: Coincident(g26,g1)
    c: Vertical(g8)
    c: Vertical(g21)
    c: Vertical(g15)
    c: Radius(g26) = 3.55
    c: Equal(g26,g19)
    c: Equal(g26,g12)
    c: Coincident(g27,g28)
    c: Coincident(g28,g29)
    c: Coincident(g29,g30)
    c: Coincident(g30,g31)
    c: Coincident(g31,g32)
    c: Coincident(g32,g27)
    c: Equal(g27, g28-g32) x5
    c: PointOnObject(g27,g33)
    c: PointOnObject(g28,g33)
    c: PointOnObject(g29,g33)
    c: PointOnObject(g30,g33)
    c: PointOnObject(g31,g33)
    c: PointOnObject(g32,g33)
    c: Coincident(g33,g2)
    c: Vertical(g29)
    c: Equal(g33,g12)
FEATURE [PartDesign::Pocket] Pocket014  label="pocket-engine-nuts"
  BaseFeature = -> Pocket013
  Length = 1.8
  Length2 = 100
  Profile = -> Sketch026
  Reversed = true
  Type = 0
  expr: Length = config.engine_screw_nut_depth
FEATURE [Sketcher::SketchObject] Sketch027
  MapMode = 5
  Placement = pos=(0,0,0) rot=(1,0,0;1.5708rad)
  Support = -> [XZ_Plane004]
  expr: Constraints[13] = config.car_floor_thickness + 2 * config.engine_radius + config.engine_lift_from_base * 2
  expr: Constraints[12] = config.car_width / 2 + config.engine_pocket_house * 0.8
  expr: Constraints[7] = config.car_floor_thickness
  expr: Constraints[23] = config.lower_car_height
  expr: Constraints[9] = config.car_width / 2 + config.engine_front_length
  sketch-geometry (9):
    g0: LineSegment StartX=-89.6 StartY=49.6 StartZ=0 EndX=-100 EndY=39.6 EndZ=0
    g1: LineSegment StartX=-100 StartY=39.6 StartZ=0 EndX=-100 EndY=49.6 EndZ=0
    g2: LineSegment StartX=-88.4 StartY=0 StartZ=0 EndX=-100 EndY=10 EndZ=0
    g3: LineSegment StartX=-100 StartY=10 StartZ=0 EndX=-100 EndY=0 EndZ=0
    g4: LineSegment StartX=-100 StartY=0 StartZ=0 EndX=-88.4 EndY=0 EndZ=0
    g5: LineSegment StartX=-89.6 StartY=49.6 StartZ=0 EndX=-100 EndY=49.6 EndZ=0
    g6: LineSegment StartX=-100 StartY=49.6 StartZ=0 EndX=-100 EndY=90 EndZ=0
    g7: LineSegment StartX=-100 StartY=90 StartZ=0 EndX=-89.6 EndY=90 EndZ=0
    g8: LineSegment StartX=-89.6 StartY=90 StartZ=0 EndX=-89.6 EndY=49.6 EndZ=0
  constraints (26):
    c: Coincident(g0,g1)
    c: Vertical(g1)
    c: PointOnObject(g2,g-1)
    c: Coincident(g2,g3)
    c: PointOnObject(g3,g-1)
    c: Coincident(g3,g4)
    c: Coincident(g4,g2)
    c: Distance(g3) = 10
    c: DistanceX(g3,g-1) = 100
    c: DistanceX(g1,g-1) = 100
    c: DistanceX(g2,g-1) = 88.4
    c: Vertical(g3)
    c: DistanceX(g0,g-1) = 89.6
    c: DistanceY(g3,g0) = 39.6
    c: Coincident(g5,g6)
    c: Coincident(g6,g7)
    c: Coincident(g7,g8)
    c: Coincident(g8,g5)
    c: Horizontal(g7)
    c: Vertical(g6)
    c: Vertical(g8)
    c: Coincident(g5,g0)
    c: Coincident(g5,g1)
    c: DistanceY(g-1,g6) = 90
    c: Horizontal(g5)
    c: DistanceY(g1,g1) = 10
FEATURE [PartDesign::Pocket] Pocket015  label="pocket-trim-engine-house001"
  BaseFeature = -> Pocket014
  Length = 5
  Length2 = 100
  Profile = -> Sketch027
  Type = 1
FEATURE [PartDesign::Mirrored] Mirrored
  MirrorPlane = -> Sketch023 [V_Axis]
FEATURE [PartDesign::Mirrored] Mirrored001
  MirrorPlane = -> Sketch022 [V_Axis]
FEATURE [Sketcher::SketchObject] Sketch028
  AttachmentOffset = pos=(0,0,10) rot=(0,0,1;0rad)
  MapMode = 5
  Placement = pos=(0,0,10) rot=(0,0,1;0rad)
  Support = -> [XY_Plane004]
  expr: Constraints[2] = config.grasscutter_placement_yaxis
  expr: AttachmentOffset.Base.z = config.car_floor_thickness
  expr: Constraints[0] = config.grasscutter_inner_radius
  sketch-geometry (1):
    g0: Circle CenterX=0 CenterY=29.3 CenterZ=0 NormalX=0 NormalY=0 NormalZ=1 AngleXU=0 Radius=7.5
  constraints (3):
    c: Radius(g0) = 7.5
    c: PointOnObject(g0,g-2)
    c: Distance(g-1,g0) = 29.3
FEATURE [Sketcher::SketchObject] Sketch029
  AttachmentOffset = pos=(0,29.3,-2) rot=(0,0,1;0rad)
  MapMode = 5
  Placement = pos=(0,29.3,-2) rot=(0,0,1;0rad)
  Support = -> [XY_Plane004]
  expr: AttachmentOffset.Base.y = config.grasscutter_placement_yaxis
  expr: Constraints[19] = config.grasscutter_screw_hole_radius
  expr: Constraints[18] = config.grasscutter_screw_radius
  sketch-geometry (13):
    g0: LineSegment [constr] StartX=11.6913 StartY=6.75 StartZ=0 EndX=-1.24e-14 EndY=13.5 EndZ=0
    g1: LineSegment [constr] StartX=-1.24e-14 StartY=13.5 StartZ=0 EndX=-11.6913 EndY=6.75 EndZ=0
    g2: LineSegment [constr] StartX=-11.6913 StartY=6.75 StartZ=0 EndX=-11.6913 EndY=-6.75 EndZ=0
    g3: LineSegment [constr] StartX=-11.6913 StartY=-6.75 StartZ=0 EndX=1.8e-15 EndY=-13.5 EndZ=0
    g4: LineSegment [constr] StartX=1.8e-15 StartY=-13.5 StartZ=0 EndX=11.6913 EndY=-6.75 EndZ=0
    g5: LineSegment [constr] StartX=11.6913 StartY=-6.75 StartZ=0 EndX=11.6913 EndY=6.75 EndZ=0
    g6: Circle [constr] CenterX=0 CenterY=0 CenterZ=0 NormalX=0 NormalY=0 NormalZ=1 AngleXU=0 Radius=13.5
    g7: Circle [constr] CenterX=-11.6913 CenterY=-6.75 CenterZ=0 NormalX=0 NormalY=0 NormalZ=1 AngleXU=0 Radius=1.52
    g8: Circle CenterX=1.8e-15 CenterY=-13.5 CenterZ=0 NormalX=0 NormalY=0 NormalZ=1 AngleXU=0 Radius=1.52
    g9: Circle [constr] CenterX=11.6913 CenterY=-6.75 CenterZ=0 NormalX=0 NormalY=0 NormalZ=1 AngleXU=0 Radius=1.52
    g10: Circle CenterX=11.6913 CenterY=6.75 CenterZ=0 NormalX=0 NormalY=0 NormalZ=1 AngleXU=0 Radius=1.52
    g11: Circle CenterX=-1.24e-14 CenterY=13.5 CenterZ=0 NormalX=0 NormalY=0 NormalZ=1 AngleXU=0 Radius=1.52
    g12: Circle CenterX=-11.6913 CenterY=6.75 CenterZ=0 NormalX=0 NormalY=0 NormalZ=1 AngleXU=0 Radius=1.52
  constraints (28):
    c: Coincident(g0,g1)
    c: Coincident(g1,g2)
    c: Coincident(g2,g3)
    c: Coincident(g3,g4)
    c: Coincident(g4,g5)
    c: Coincident(g5,g0)
    c: Equal(g0, g1-g5) x5
    c: PointOnObject(g0,g6)
    c: PointOnObject(g1,g6)
    c: PointOnObject(g2,g6)
    c: PointOnObject(g3,g6)
    c: PointOnObject(g4,g6)
    c: PointOnObject(g5,g6)
    c: Coincident(g6,g-1)
    c: Radius(g6) = 13.5
    c: Radius(g9) = 1.52
    c: Equal(g9,g8)
    c: Equal(g9,g7)
    c: Equal(g9,g12)
    c: Equal(g9,g11)
    c: Equal(g9,g10)
    c: Coincident(g3,g8)
    c: Coincident(g2,g7)
    c: Coincident(g1,g12)
    c: Coincident(g4,g9)
    c: Coincident(g1,g11)
    c: Coincident(g10,g0)
    c: Vertical(g2)
FEATURE [Sketcher::SketchObject] Sketch030
  AttachmentOffset = pos=(0,29.3,0) rot=(0,0,1;0rad)
  MapMode = 5
  Placement = pos=(0,29.3,0) rot=(0,0,1;0rad)
  Support = -> [XY_Plane004]
  expr: AttachmentOffset.Base.y = config.grasscutter_placement_yaxis
  expr: Constraints[24] = config.grasscutter_screw_nut_radius
  expr: Constraints[18] = config.grasscutter_screw_radius
  sketch-geometry (11):
    g0: LineSegment [constr] StartX=11.6913 StartY=6.75 StartZ=0 EndX=-1.24e-14 EndY=13.5 EndZ=0
    g1: LineSegment [constr] StartX=-1.24e-14 StartY=13.5 StartZ=0 EndX=-11.6913 EndY=6.75 EndZ=0
    g2: LineSegment [constr] StartX=-11.6913 StartY=6.75 StartZ=0 EndX=-11.6913 EndY=-6.75 EndZ=0
    g3: LineSegment [constr] StartX=-11.6913 StartY=-6.75 StartZ=0 EndX=1.8e-15 EndY=-13.5 EndZ=0
    g4: LineSegment [constr] StartX=1.8e-15 StartY=-13.5 StartZ=0 EndX=11.6913 EndY=-6.75 EndZ=0
    g5: LineSegment [constr] StartX=11.6913 StartY=-6.75 StartZ=0 EndX=11.6913 EndY=6.75 EndZ=0
    g6: Circle [constr] CenterX=0 CenterY=0 CenterZ=0 NormalX=0 NormalY=0 NormalZ=1 AngleXU=0 Radius=13.5
    g7: Circle CenterX=1.8e-15 CenterY=-13.5 CenterZ=0 NormalX=0 NormalY=0 NormalZ=1 AngleXU=0 Radius=2.5
    g8: Circle CenterX=11.6913 CenterY=6.75 CenterZ=0 NormalX=0 NormalY=0 NormalZ=1 AngleXU=0 Radius=2.5
    g9: Circle CenterX=-1.24e-14 CenterY=13.5 CenterZ=0 NormalX=0 NormalY=0 NormalZ=1 AngleXU=0 Radius=2.5
    g10: Circle CenterX=-11.6913 CenterY=6.75 CenterZ=0 NormalX=0 NormalY=0 NormalZ=1 AngleXU=0 Radius=2.5
  constraints (24):
    c: Coincident(g0,g1)
    c: Coincident(g1,g2)
    c: Coincident(g2,g3)
    c: Coincident(g3,g4)
    c: Coincident(g4,g5)
    c: Coincident(g5,g0)
    c: Equal(g0, g1-g5) x5
    c: PointOnObject(g0,g6)
    c: PointOnObject(g1,g6)
    c: PointOnObject(g2,g6)
    c: PointOnObject(g3,g6)
    c: PointOnObject(g4,g6)
    c: PointOnObject(g5,g6)
    c: Coincident(g6,g-1)
    c: Radius(g6) = 13.5
    c: Coincident(g3,g7)
    c: Coincident(g1,g10)
    c: Coincident(g1,g9)
    c: Coincident(g8,g0)
    c: Vertical(g2)
    c: Radius(g8) = 2.5
    c: Equal(g8,g9)
    c: Equal(g9,g10)
    c: Equal(g7,g8)
FEATURE [Sketcher::SketchObject] Sketch031
  MapMode = 5
  Support = -> [XY_Plane005]
  expr: Constraints[12] = config.rpi_length / 2
  expr: Constraints[10] = config.rpi_placement_yaxis
  expr: Constraints[9] = config.rpi_width
  expr: Constraints[8] = config.rpi_length
  sketch-geometry (5):
    g0: LineSegment StartX=-45 StartY=113 StartZ=0 EndX=45 EndY=113 EndZ=0
    g1: LineSegment StartX=45 StartY=113 StartZ=0 EndX=45 EndY=53 EndZ=0
    g2: LineSegment StartX=45 StartY=53 StartZ=0 EndX=-45 EndY=53 EndZ=0
    g3: LineSegment StartX=-45 StartY=53 StartZ=0 EndX=-45 EndY=113 EndZ=0
    g4: GeomPoint X=0 Y=53 Z=0
  constraints (14):
    c: Coincident(g0,g1)
    c: Coincident(g1,g2)
    c: Coincident(g2,g3)
    c: Coincident(g3,g0)
    c: Horizontal(g0)
    c: Horizontal(g2)
    c: Vertical(g1)
    c: Vertical(g3)
    c: Distance(g2) = 90
    c: Distance(g1) = 60
    c: DistanceY(g-1,g2) = 53
    c: PointOnObject(g4,g2)
    c: Distance(g2,g4) = 45
    c: PointOnObject(g4,g-2)
FEATURE [PartDesign::Pad] Pad008
  Length = 30
  Length2 = 100
  Profile = -> Sketch031
  Type = 0
  expr: Length = config.rpi_height
FEATURE [PartDesign::Body] Body005  label="body-rpi"
  Group = -> [Sketch031,Pad008]
  Origin = -> Origin005
  Tip = -> Pad008
FEATURE [Sketcher::SketchObject] Sketch033
  AttachmentOffset = pos=(0,29.3,0) rot=(0,0,1;0rad)
  MapMode = 5
  Placement = pos=(0,29.3,0) rot=(0,0,1;0rad)
  Support = -> [XY_Plane004]
  expr: AttachmentOffset.Base.y = config.grasscutter_placement_yaxis
  expr: AttachmentOffset.Base.x = 0
  expr: Constraints[3] = config.grasscutter_motor_radius + config.car_wall_thickness
  expr: Constraints[1] = config.grasscutter_motor_radius
  sketch-geometry (8):
    g0: Circle [constr] CenterX=0 CenterY=0 CenterZ=0 NormalX=0 NormalY=0 NormalZ=1 AngleXU=0 Radius=18.7
    g1: Circle [constr] CenterX=0 CenterY=0 CenterZ=0 NormalX=0 NormalY=0 NormalZ=1 AngleXU=0 Radius=23.7
    g2: ArcOfCircle CenterX=0 CenterY=0 CenterZ=0 NormalX=0 NormalY=0 NormalZ=1 AngleXU=0 Radius=18.7 StartAngle=0.523599 EndAngle=1.0472
    g3: ArcOfCircle CenterX=0 CenterY=0 CenterZ=0 NormalX=0 NormalY=0 NormalZ=1 AngleXU=0 Radius=23.7 StartAngle=0.523599 EndAngle=1.0472
    g4: LineSegment StartX=16.1947 StartY=9.35 StartZ=0 EndX=20.5248 EndY=11.85 EndZ=0
    g5: LineSegment StartX=9.35 StartY=16.1947 StartZ=0 EndX=11.85 EndY=20.5248 EndZ=0
    g6: LineSegment [constr] StartX=0 StartY=0 StartZ=0 EndX=16.1947 EndY=9.35 EndZ=0
    g7: LineSegment [constr] StartX=0 StartY=0 StartZ=0 EndX=9.35 EndY=16.1947 EndZ=0
  constraints (20):
    c: Coincident(g0,g-1)
    c: Radius(g0) = 18.7
    c: Coincident(g1,g0)
    c: Radius(g1) = 23.7
    c: PointOnObject(g2,g0)
    c: PointOnObject(g3,g1)
    c: Coincident(g3,g4)
    c: Coincident(g2,g4)
    c: Coincident(g2,g5)
    c: Coincident(g3,g5)
    c: Coincident(g6,g2)
    c: Coincident(g6,g2)
    c: Coincident(g7,g2)
    c: Coincident(g7,g2)
    c: Angle(g6,g7) = 0.523599
    c: Parallel(g5,g7)
    c: Parallel(g4,g6)
    c: Coincident(g0,g2)
    c: Coincident(g0,g3)
    c: Angle(g7,g-2) = 0.523599
FEATURE [PartDesign::Pad] Pad009
  BaseFeature = -> Pocket015
  Length = 50
  Length2 = 100
  Profile = -> Sketch033
  Type = 0
  expr: Length = config.grasscutter_wall_height
FEATURE [PartDesign::PolarPattern] PolarPattern001  label="pad-grasscutter-walls"
  Angle = 360
  Axis = -> Sketch033 [N_Axis]
  BaseFeature = -> Pad009
  Occurrences = 4
  Originals = -> [Pad009]
FEATURE [Sketcher::SketchObject] Sketch034
  MapMode = 5
  Support = -> [XY_Plane004]
  expr: Constraints[35] = config.battery_placement_yaxis - 1mm
  expr: Constraints[34] = -(config.battery_length / 2 + 1mm)
  expr: Constraints[31] = config.battery_width / 3
  expr: Constraints[30] = config.car_wall_thickness
  expr: Constraints[16] = config.battery_width / 3
  expr: Constraints[15] = config.battery_length / 2 + 1mm
  expr: Constraints[14] = config.battery_placement_yaxis + config.battery_width + 1mm
  expr: Constraints[13] = config.car_wall_thickness
  expr: Constraints[11] = config.car_wall_thickness
  sketch-geometry (12):
    g0: LineSegment StartX=-57 StartY=-6.96667 StartZ=0 EndX=-57 EndY=6.6 EndZ=0
    g1: LineSegment StartX=-57 StartY=6.6 StartZ=0 EndX=-43.4333 EndY=6.6 EndZ=0
    g2: LineSegment StartX=-43.4333 StartY=6.6 StartZ=0 EndX=-43.4333 EndY=11.6 EndZ=0
    g3: LineSegment StartX=-43.4333 StartY=11.6 StartZ=0 EndX=-62 EndY=11.6 EndZ=0
    g4: LineSegment StartX=-62 StartY=-6.96667 StartZ=0 EndX=-62 EndY=11.6 EndZ=0
    g5: LineSegment StartX=-62 StartY=-6.96667 StartZ=0 EndX=-57 EndY=-6.96667 EndZ=0
    g6: LineSegment StartX=-57 StartY=-37.5333 StartZ=0 EndX=-57 EndY=-51.1 EndZ=0
    g7: LineSegment StartX=-57 StartY=-51.1 StartZ=0 EndX=-43.4333 EndY=-51.1 EndZ=0
    g8: LineSegment StartX=-43.4333 StartY=-51.1 StartZ=0 EndX=-43.4333 EndY=-56.1 EndZ=0
    g9: LineSegment StartX=-43.4333 StartY=-56.1 StartZ=0 EndX=-62 EndY=-56.1 EndZ=0
    g10: LineSegment StartX=-62 StartY=-56.1 StartZ=0 EndX=-62 EndY=-37.5333 EndZ=0
    g11: LineSegment StartX=-62 StartY=-37.5333 StartZ=0 EndX=-57 EndY=-37.5333 EndZ=0
  constraints (36):
    c: Vertical(g0)
    c: Coincident(g0,g1)
    c: Horizontal(g1)
    c: Coincident(g1,g2)
    c: Vertical(g2)
    c: Coincident(g2,g3)
    c: Coincident(g4,g3)
    c: Vertical(g4)
    c: Coincident(g4,g5)
    c: Coincident(g5,g0)
    c: Horizontal(g5)
    c: Distance(g2) = 5
    c: Horizontal(g3)
    c: Distance(g5) = 5
    c: DistanceY(g-1,g0) = 6.6
    c: DistanceX(g0,g-1) = 57
    c: Distance(g4) = 18.5667
    c: Equal(g4,g3)
    c: Vertical(g6)
    c: Coincident(g6,g7)
    c: Horizontal(g7)
    c: Coincident(g7,g8)
    c: Vertical(g8)
    c: Coincident(g8,g9)
    c: Horizontal(g9)
    c: Coincident(g9,g10)
    c: Vertical(g10)
    c: Coincident(g10,g11)
    c: Coincident(g11,g6)
    c: Horizontal(g11)
    c: Distance(g11) = 5
    c: Distance(g10) = 18.5667
    c: Equal(g8,g11)
    c: Equal(g10,g9)
    c: DistanceX(g-2,g6) = -57
    c: DistanceY(g-1,g6) = -51.1
FEATURE [Part::Feature] Part__Feature  label="Raspberry Pi Camera (G) 160\X\B0"
  shape: bbox 22.03 x 2.743 x 21.76 mm, 9 faces (baked)
FEATURE [Part::Feature] Part__Feature001  label="Raspberry Pi Camera (G) 160\X\B001"
  shape: bbox 21.76 x 2.743 x 22.03 mm, 9 faces (baked)
FEATURE [Part::Feature] Part__Feature002  label="Raspberry Pi Camera (G) 160\X\B002"
  shape: bbox 41.58 x 19.13 x 41.58 mm, 43 faces (baked)
FEATURE [Part::Feature] Part__Feature003  label="Raspberry Pi Camera (G) 160\X\B003"
  shape: bbox 29.7 x 4.464 x 29.7 mm, 6 faces (baked)
FEATURE [Part::Feature] Part__Feature004  label="Raspberry Pi Camera (G) 160\X\B004"
  shape: bbox 47.7 x 34.03 x 47.38 mm, 15 faces (baked)
FEATURE [Part::Feature] Part__Feature005  label="Raspberry Pi Camera (G) 160\X\B005"
  shape: bbox 47.52 x 0.2 x 47.52 mm, 6 faces (baked)
FEATURE [Part::Feature] Part__Feature006  label="Raspberry Pi Camera (G) 160\X\B006"
  shape: bbox 72.78 x 3.8 x 72.78 mm, 10 faces (baked)
FEATURE [Part::Feature] Part__Feature007  label="Raspberry Pi Camera (G) 160\X\B007"
  shape: bbox 72.78 x 3.8 x 72.78 mm, 10 faces (baked)
FEATURE [App::Part] Shapes  label="shape-rpi-camera"
  Group = -> [Part__Feature,Part__Feature001,Part__Feature002,Part__Feature003,Part__Feature004,Part__Feature005,Part__Feature006,Part__Feature007]
  Origin = -> Origin006
  Placement = pos=(0,120,75) rot=(1,0,0;-0.261799rad)
  expr: Placement.Base.y = config.car_length / 2mm
FEATURE [Spreadsheet::Sheet] Spreadsheet001  label="camera"
  cells = A1=CAMERA; A2=camera_placement_yaxis; B2==120mm; A3=camera_placement_zaxis; B3==60mm; A4=camera_support_start_zaxis; B4==50mm; A5=camera_tilt_angle; B5=15; A6=camera_width; B6==24mm; A7=camera_height; B7==25mm; A8=camera_lens_length; B8==15mm; A9=camera_lens_radius; B9==7.5mm; A10=camera_screw1_height; B10==9.5mm; A11=camera_screw2_height; B11==9.5mm + 12.5mm; A12=camera_screw_dist_apart; B12==21mm; A13=camera_screw_radius; B13==1mm; A14=camera_screw_depth; B14==3mm; C14=length of taps to hold the camera
FEATURE [Mesh::Feature] RPI_WW_Back_01  label="RPI-WW-Back_01"
  Placement = pos=(0,200,0) rot=(0,0,1;0rad)
FEATURE [Mesh::Feature] wide_angle_front
  Placement = pos=(0,200,0) rot=(0,0,1;0rad)
FEATURE [Sketcher::SketchObject] Sketch036
  MapMode = 5
  Placement = pos=(0,0,0) rot=(0.57735,0.57735,0.57735;2.0944rad)
  Support = -> [YZ_Plane007]
FEATURE [PartDesign::Body] Body006  label="body-camera-case"
  Group = -> [Sketch036]
  Origin = -> Origin007
FEATURE [PartDesign::Plane] DatumPlane
  AttachmentOffset = pos=(0,0,-85.8846) rot=(-1,0,0;0.261799rad)
  Length = 235.903
  MapMode = 5
  Placement = pos=(0,85.8846,1.91e-14) rot=(1,0,0;1.309rad)
  ResizeMode = 0
  Support = -> [XZ_Plane004]
  Width = 197.027
  expr: AttachmentOffset.Base.z = 5mm + config.car_wall_thickness - (config.car_length / 2 - config.lower_car_height / tan(75))
FEATURE [Sketcher::SketchObject] Sketch043
  MapMode = 5
  Placement = pos=(0,85.8846,1.78e-14) rot=(1,0,0;1.309rad)
  Support = -> [DatumPlane]
  expr: Constraints[22] = config.camera_screw_dist_apart
  expr: Constraints[10] = config.camera_screw2_height
  expr: Constraints[17] = config.camera_screw_radius
  expr: Constraints[9] = config.camera_screw1_height
  expr: Constraints[12] = config.camera_lens_radius
  expr: Constraints[11] = 24mm - 9.5mm
  sketch-geometry (12):
    g0: Circle CenterX=0 CenterY=77 CenterZ=0 NormalX=0 NormalY=0 NormalZ=1 AngleXU=0 Radius=7.5
    g1: LineSegment [constr] StartX=-10.5 StartY=72 StartZ=0 EndX=10.5 EndY=72 EndZ=0
    g2: LineSegment [constr] StartX=10.5 StartY=72 StartZ=0 EndX=10.5 EndY=84.5 EndZ=0
    g3: LineSegment [constr] StartX=10.5 StartY=84.5 StartZ=0 EndX=-10.5 EndY=84.5 EndZ=0
    g4: LineSegment [constr] StartX=-10.5 StartY=84.5 StartZ=0 EndX=-10.5 EndY=72 EndZ=0
    g5: LineSegment [constr] StartX=-10.5 StartY=62.5 StartZ=0 EndX=10.5 EndY=62.5 EndZ=0
    g6: Circle CenterX=-10.5 CenterY=84.5 CenterZ=0 NormalX=0 NormalY=0 NormalZ=1 AngleXU=0 Radius=1.1
    g7: Circle CenterX=-10.5 CenterY=72 CenterZ=0 NormalX=0 NormalY=0 NormalZ=1 AngleXU=0 Radius=1.1
    g8: Circle CenterX=10.5 CenterY=72 CenterZ=0 NormalX=0 NormalY=0 NormalZ=1 AngleXU=0 Radius=1.1
    g9: Circle CenterX=10.5 CenterY=84.5 CenterZ=0 NormalX=0 NormalY=0 NormalZ=1 AngleXU=0 Radius=1.1
    g10: LineSegment [constr] StartX=-10.5 StartY=72 StartZ=0 EndX=-10.5 EndY=62.5 EndZ=0
    g11: LineSegment [constr] StartX=10.5 StartY=72 StartZ=0 EndX=10.5 EndY=62.5 EndZ=0
  constraints (30):
    c: PointOnObject(g0,g-2)
    c: Coincident(g1,g2)
    c: Coincident(g2,g3)
    c: Coincident(g3,g4)
    c: Coincident(g4,g1)
    c: Horizontal(g1)
    c: Vertical(g2)
    c: Vertical(g4)
    c: Horizontal(g5)
    c: DistanceY(g5,g1) = 9.5
    c: DistanceY(g5,g3) = 22
    c: DistanceY(g5,g0) = 14.5
    c: Radius(g0) = 7.5
    c: Coincident(g6,g3)
    c: Coincident(g7,g1)
    c: Coincident(g8,g1)
    c: Coincident(g9,g2)
    c: Radius(g9) = 1.1
    c: Equal(g9,g6)
    c: Equal(g9,g7)
    c: Equal(g9,g8)
    c: Symmetric(g6,g9,g-2)
    c: Distance(g3) = 21
    c: DistanceY(g-1,g5) = 62.5
    c: Equal(g5,g1)
    c: Coincident(g10,g7)
    c: Coincident(g10,g5)
    c: Vertical(g10)
    c: Coincident(g11,g8)
    c: Coincident(g11,g5)
FEATURE [Sketcher::SketchObject] Sketch045
  AttachmentOffset = pos=(0,0,-80) rot=(0,0,1;0rad)
  MapMode = 5
  Placement = pos=(-80,1.78e-14,-1.78e-14) rot=(0.57735,0.57735,0.57735;2.0944rad)
  Support = -> [YZ_Plane004]
  expr: Constraints[13] = config.fan_screw_sepdist
  expr: Constraints[19] = config.fan_screw_hole_radius
  expr: AttachmentOffset.Base.z = -config.car_width / 2
  expr: AttachmentOffset.Base.y = 0
  expr: AttachmentOffset.Base.x = 0
  expr: Constraints[9] = config.fan_screw_sepdist / 2
  expr: Constraints[10] = config.lower_car_height - 10mm
  sketch-geometry (8):
    g0: Circle CenterX=20 CenterY=80 CenterZ=0 NormalX=0 NormalY=0 NormalZ=1 AngleXU=0 Radius=1.65
    g1: Circle CenterX=20 CenterY=40 CenterZ=0 NormalX=0 NormalY=0 NormalZ=1 AngleXU=0 Radius=1.65
    g2: LineSegment [constr] StartX=-3.7e-15 StartY=80 StartZ=0 EndX=20 EndY=80 EndZ=0
    g3: LineSegment [constr] StartX=20 StartY=80 StartZ=0 EndX=20 EndY=40 EndZ=0
    g4: LineSegment [constr] StartX=20 StartY=40 StartZ=0 EndX=-3.6e-15 EndY=40 EndZ=0
    g5: LineSegment [constr] StartX=-3.7e-15 StartY=40 StartZ=0 EndX=-3.7e-15 EndY=80 EndZ=0
    g6: ArcOfCircle CenterX=0 CenterY=60 CenterZ=0 NormalX=0 NormalY=0 NormalZ=1 AngleXU=0 Radius=20 StartAngle=4.71239 EndAngle=7.85398
    g7: LineSegment StartX=-3.7e-15 StartY=80 StartZ=0 EndX=-3.7e-15 EndY=40 EndZ=0
  constraints (21):
    c: Coincident(g2,g3)
    c: Coincident(g3,g4)
    c: Coincident(g5,g2)
    c: Horizontal(g2)
    c: Horizontal(g4)
    c: Vertical(g3)
    c: Vertical(g5)
    c: Coincident(g3,g1)
    c: Coincident(g0,g2)
    c: Distance(g2) = 20
    c: DistanceY(g-1,g0) = 80
    c: PointOnObject(g2,g-2)
    c: Coincident(g5,g4)
    c: Distance(g3) = 40
    c: PointOnObject(g6,g5)
    c: Coincident(g6,g4)
    c: Coincident(g6,g2)
    c: Coincident(g7,g6)
    c: Coincident(g7,g6)
    c: Radius(g0) = 1.65
    c: Equal(g0,g1)
FEATURE [PartDesign::Pocket] Pocket022  label="pocket-fan"
  BaseFeature = -> PolarPattern001
  Length = 5
  Length2 = 100
  Profile = -> Sketch045
  Reversed = true
  Type = 0
  expr: Length = config.car_wall_thickness
FEATURE [PartDesign::MultiTransform] MultiTransform  label="Mirror-walls"
  BaseFeature = -> Pocket022
  Originals = -> [Pad007,Pocket015,Pocket012,Pocket013,Pocket014,Pocket011,Pocket022]
  Transformations = -> [Mirrored,Mirrored001]
FEATURE [PartDesign::Pocket] Pocket016  label="pocket-grasscutter-inner-radius"
  BaseFeature = -> MultiTransform
  Length = 5
  Length2 = 100
  Profile = -> Sketch028
  Type = 1
FEATURE [PartDesign::Pocket] Pocket017  label="pocket-grasscutter-screws"
  BaseFeature = -> Pocket016
  Length = 5
  Length2 = 100
  Profile = -> Sketch029
  Reversed = true
  Type = 1
FEATURE [PartDesign::Pocket] Pocket018  label="pocket-grasscutter-screw-head-hole"
  BaseFeature = -> Pocket017
  Length = 1
  Length2 = 100
  Profile = -> Sketch030
  Reversed = true
  Type = 0
  expr: Length = config.grasscutter_screw_nut_depth
FEATURE [PartDesign::Pad] Pad010  label="pad-battery-walls"
  BaseFeature = -> Pocket018
  Length = 50
  Length2 = 100
  Profile = -> Sketch034
  Type = 0
  expr: Length = config.grasscutter_wall_height
FEATURE [PartDesign::Mirrored] Mirrored002  label="mirror-battery-walls"
  BaseFeature = -> Pad010
  MirrorPlane = -> Sketch034 [V_Axis]
  Originals = -> [Pad010]
FEATURE [Sketcher::SketchObject] Sketch037
  MapMode = 5
  Placement = pos=(0,0,0) rot=(0.57735,0.57735,0.57735;2.0944rad)
  Support = -> [YZ_Plane004]
  expr: Constraints[6] = config.camera_support_start_zaxis
  expr: Constraints[2] = config.camera_placement_yaxis - config.car_wall_thickness
  expr: Constraints[16] = config.lower_car_height
  expr: Constraints[3] = config.car_wall_thickness
  expr: Constraints[5] = 90 + config.camera_tilt_angle
  sketch-geometry (8):
    g0: LineSegment StartX=120 StartY=50 StartZ=0 EndX=129.331 EndY=84.8236 EndZ=0
    g1: LineSegment StartX=115 StartY=50 StartZ=0 EndX=120 EndY=50 EndZ=0
    g2: LineSegment [constr] StartX=102.248 StartY=61.0222 StartZ=0 EndX=121.566 EndY=55.8458 EndZ=0
    g3: LineSegment StartX=102.248 StartY=61.0222 StartZ=0 EndX=115 EndY=50 EndZ=0
    g4: LineSegment StartX=102.248 StartY=61.0222 StartZ=0 EndX=110.012 EndY=90 EndZ=0
    g5: LineSegment [constr] StartX=110.012 StartY=90 StartZ=0 EndX=129.331 EndY=84.8236 EndZ=0
    g6: LineSegment StartX=110.012 StartY=90 StartZ=0 EndX=129.331 EndY=90 EndZ=0
    g7: LineSegment StartX=129.331 StartY=90 StartZ=0 EndX=129.331 EndY=84.8236 EndZ=0
  constraints (23):
    c: Coincident(g1,g0)
    c: Horizontal(g1)
    c: DistanceX(g-1,g1) = 115
    c: Distance(g1) = 5
    c: PointOnObject(g2,g0)
    c: Angle(g0,g1) = 1.8326
    c: DistanceY(g-1,g0) = 50
    c: Coincident(g3,g1)
    c: Coincident(g3,g4)
    c: Parallel(g4,g0)
    c: Coincident(g2,g3)
    c: Distance(g4) = 30
    c: Coincident(g5,g0)
    c: Angle(g5,g0) = 1.5708
    c: Angle(g2,g4) = 1.5708
    c: Distance(g5) = 20
    c: DistanceY(g-1,g4) = 90
    c: Coincident(g4,g5)
    c: Coincident(g4,g6)
    c: Horizontal(g6)
    c: Coincident(g6,g7)
    c: Coincident(g7,g0)
    c: Vertical(g7)
FEATURE [PartDesign::Pad] Pad011  label="pad-camera-house"
  BaseFeature = -> Mirrored002
  Length = 17
  Length2 = 17
  Profile = -> Sketch037
  Type = 4
  expr: Length2 = config.camera_width / 2 + 5mm
  expr: Length = config.camera_width / 2 + 5mm
FEATURE [Sketcher::SketchObject] Sketch046
  MapMode = 5
  Placement = pos=(0,85.8846,1.78e-14) rot=(1,0,0;1.309rad)
  Support = -> [DatumPlane]
  expr: Constraints[22] = 61.89mm - 10mm
  expr: AttachmentOffset.Base.z = 0
  expr: AttachmentOffset.Base.x = 0
  expr: Constraints[15] = config.camera_width + 1mm
  sketch-geometry (8):
    g0: LineSegment StartX=-12.5 StartY=91.89 StartZ=0 EndX=-12.5 EndY=61.89 EndZ=0
    g1: LineSegment StartX=-12.5 StartY=61.89 StartZ=0 EndX=-10 EndY=61.89 EndZ=0
    g2: LineSegment StartX=-10 StartY=61.89 StartZ=0 EndX=-10 EndY=51.89 EndZ=0
    g3: LineSegment StartX=-10 StartY=51.89 StartZ=0 EndX=10 EndY=51.89 EndZ=0
    g4: LineSegment StartX=10 StartY=51.89 StartZ=0 EndX=10 EndY=61.89 EndZ=0
    g5: LineSegment StartX=10 StartY=61.89 StartZ=0 EndX=12.5 EndY=61.89 EndZ=0
    g6: LineSegment StartX=12.5 StartY=61.89 StartZ=0 EndX=12.5 EndY=91.89 EndZ=0
    g7: LineSegment StartX=12.5 StartY=91.89 StartZ=0 EndX=-12.5 EndY=91.89 EndZ=0
  constraints (23):
    c: Vertical(g0)
    c: Coincident(g0,g1)
    c: Horizontal(g1)
    c: Coincident(g1,g2)
    c: Vertical(g2)
    c: Coincident(g2,g3)
    c: Horizontal(g3)
    c: Coincident(g3,g4)
    c: Vertical(g4)
    c: Coincident(g4,g5)
    c: Horizontal(g5)
    c: Coincident(g5,g6)
    c: Vertical(g6)
    c: Coincident(g6,g7)
    c: Coincident(g7,g0)
    c: Distance(g7) = 25
    c: Distance(g0) = 30
    c: Distance(g2) = 10
    c: Symmetric(g0,g6,g-2)
    c: Equal(g6,g0)
    c: Equal(g1,g5)
    c: Distance(g3) = 20
    c: DistanceY(g-1,g3) = 51.89
FEATURE [PartDesign::Pocket] Pocket023  label="pocket-camera-house"
  BaseFeature = -> Pad011
  Length = 7
  Length2 = 100
  Profile = -> Sketch046
  Type = 0
  expr: Length = 20mm - config.camera_lens_length
FEATURE [PartDesign::Pocket] Pocket021  label="pocket-screw-lens"
  BaseFeature = -> Pocket023
  Length = 5
  Length2 = 100
  Profile = -> Sketch043
  Type = 1
FEATURE [PartDesign::Body] Body004  label="body-full"
  Group = -> [Sketch021,Pad006,Sketch022,Pad007,Sketch023,Pocket011,Sketch024,Pocket012,Sketch025,Pocket013,Sketch026,Pocket014,Sketch027,Pocket015,Mirrored,Mirrored001,Sketch028,Sketch033,Pad009,PolarPattern001,Sketch034,Sketch037,DatumPlane,Sketch043,Sketch045,Pocket022,Sketch046,MultiTransform,Pocket016,Pocket017,Pocket018,Pad010,Mirrored002,Pad011,Pocket023,Pocket021,Sketch030,Sketch029]
  Origin = -> Origin004
  Tip = -> Pocket022
FEATURE [Sketcher::SketchObject] Sketch047
  MapMode = 5
  Support = -> [XY_Plane008]
  expr: Constraints[19] = 7.5 + 3.5
  expr: Constraints[13] = 18 / 2
  sketch-geometry (7):
    g0: LineSegment StartX=0 StartY=0 StartZ=0 EndX=36 EndY=0 EndZ=0
    g1: LineSegment StartX=36 StartY=0 StartZ=0 EndX=36 EndY=18 EndZ=0
    g2: LineSegment StartX=36 StartY=18 StartZ=0 EndX=0 EndY=18 EndZ=0
    g3: LineSegment StartX=0 StartY=18 StartZ=0 EndX=0 EndY=0 EndZ=0
    g4: LineSegment [constr] StartX=36 StartY=9 StartZ=0 EndX=0 EndY=9 EndZ=0
    g5: Circle CenterX=11 CenterY=9 CenterZ=0 NormalX=0 NormalY=0 NormalZ=1 AngleXU=0 Radius=3.5
    g6: Circle CenterX=25 CenterY=9 CenterZ=0 NormalX=0 NormalY=0 NormalZ=1 AngleXU=0 Radius=3.5
  constraints (21):
    c: Coincident(g0,g1)
    c: Coincident(g1,g2)
    c: Coincident(g2,g3)
    c: Coincident(g3,g0)
    c: Horizontal(g0)
    c: Horizontal(g2)
    c: Vertical(g1)
    c: Vertical(g3)
    c: Coincident(g0,g-1)
    c: Distance(g2) = 36
    c: Distance(g3) = 18
    c: PointOnObject(g4,g1)
    c: Horizontal(g4)
    c: Distance(g0,g4) = 9
    c: PointOnObject(g5,g4)
    c: PointOnObject(g6,g4)
    c: Radius(g6) = 3.5
    c: Equal(g6,g5)
    c: Distance(g6,g4) = 11
    c: Distance(g5,g4) = 11
    c: PointOnObject(g4,g3)
FEATURE [PartDesign::Pad] Pad012
  Length = 1
  Length2 = 100
  Profile = -> Sketch047
  Type = 0
FEATURE [PartDesign::Body] Body007  label="Body-knife-blade"
  Group = -> [Sketch047,Pad012]
  Origin = -> Origin008
  Tip = -> Pad012
FEATURE [Spreadsheet::Sheet] Spreadsheet002  label="knife"
  cells = A1=NAME; B1=VALUE; A2=knife_length; B2==36mm; A3=knife_width; B3==18mm; A4=knife_height; B4==1mm; A5=knife_screwhole_radius; B5==3.5mm; A6=knife_screwhole_sep; B6==6.8mm; A8=cutter_radius; B8==75mm; A9=cutter_width; B9==18mm; A10=cutter_height; B10==6mm; A11=cutter_hex_radius; B11==6.85mm; A12=cutter_hex_height; B12==5.1mm
FEATURE [PartDesign::Body] Body008
  Origin = -> Origin009
FEATURE [Sketcher::SketchObject] Sketch048
  MapMode = 5
  Support = -> [XY_Plane010]
  sketch-geometry (5):
    g0: Circle [constr] CenterX=0 CenterY=0 CenterZ=0 NormalX=0 NormalY=0 NormalZ=1 AngleXU=0 Radius=68.1362
    g1: LineSegment [constr] StartX=-157.036 StartY=14.7783 StartZ=0 EndX=191.061 EndY=14.7783 EndZ=0
    g2: LineSegment [constr] StartX=191.061 StartY=14.7783 StartZ=0 EndX=191.061 EndY=-14.26 EndZ=0
    g3: LineSegment [constr] StartX=191.061 StartY=-14.26 StartZ=0 EndX=-157.036 EndY=-14.26 EndZ=0
    g4: LineSegment [constr] StartX=-157.036 StartY=-14.26 StartZ=0 EndX=-157.036 EndY=14.7783 EndZ=0
  constraints (9):
    c: Coincident(g0,g-1)
    c: Coincident(g1,g2)
    c: Coincident(g2,g3)
    c: Coincident(g3,g4)
    c: Coincident(g4,g1)
    c: Horizontal(g1)
    c: Horizontal(g3)
    c: Vertical(g2)
    c: Vertical(g4)
FEATURE [PartDesign::Body] Body009
  Group = -> [Sketch048]
  Origin = -> Origin010
